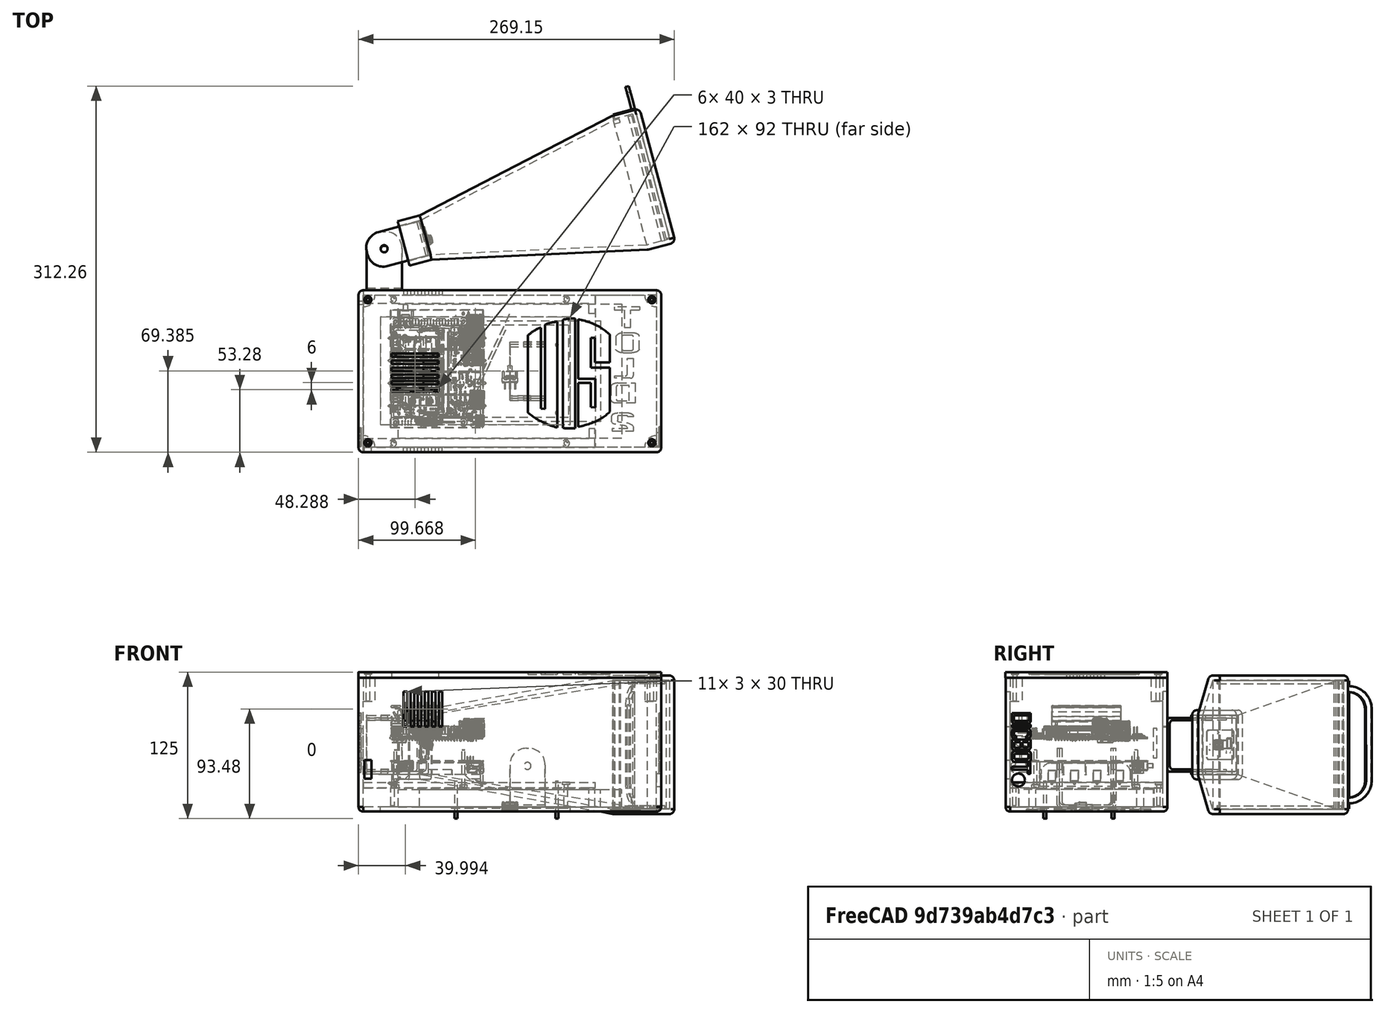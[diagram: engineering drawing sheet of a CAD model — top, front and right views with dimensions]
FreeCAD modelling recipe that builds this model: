
FCSTD DOCUMENT  (FreeCAD 0.20R)
Label: SUENCAPSULADO
License: All rights reserved
LicenseURL: http://en.wikipedia.org/wiki/All_rights_reserved
objects: Sketcher::SketchObject×38, PartDesign::Pocket×16, PartDesign::Pad×15, PartDesign::Body×9, Part::Feature×9, App::Part×6, PartDesign::Fillet×6, PartDesign::Hole×5, PartDesign::Thickness×2, Part::Compound×2, PartDesign::Plane×2
note: 148 computed .brp shape members not serialized (recipe doc carries the construction recipe); baked Part::Feature solids carry a one-line shape summary decoded from their .brp

FEATURE [Sketcher::SketchObject] Sketch
  FullyConstrained = true
  MapMode = 5
  Support = -> [XY_Plane001]
  sketch-geometry (4):
    g0: LineSegment StartX=-125 StartY=65 StartZ=0 EndX=125 EndY=65 EndZ=0
    g1: LineSegment StartX=125 StartY=65 StartZ=0 EndX=125 EndY=-65 EndZ=0
    g2: LineSegment StartX=125 StartY=-65 StartZ=0 EndX=-125 EndY=-65 EndZ=0
    g3: LineSegment StartX=-125 StartY=-65 StartZ=0 EndX=-125 EndY=65 EndZ=0
  constraints (11):
    c: Coincident(g0,g1)
    c: Coincident(g1,g2)
    c: Coincident(g2,g3)
    c: Coincident(g3,g0)
    c: Horizontal(g0)
    c: Horizontal(g2)
    c: Vertical(g1)
    c: Vertical(g3)
    c: Symmetric(g1,g0,g-1)
    c: DistanceX(g2,g2) = 250
    c: DistanceY(g1,g1) = 130
FEATURE [PartDesign::Pad] Pad
  Direction = (0,0,1)
  Length = 110
  Length2 = 10
  Profile = -> Sketch
  ReferenceAxis = -> Sketch [N_Axis]
  Type = 0
FEATURE [Sketcher::SketchObject] Sketch001
  FullyConstrained = true
  MapMode = 5
  Support = -> [XY_Plane003]
  sketch-geometry (8):
    g0: LineSegment StartX=-95.25 StartY=57.3 StartZ=0 EndX=95.25 EndY=57.3 EndZ=0
    g1: LineSegment StartX=95.25 StartY=57.3 StartZ=0 EndX=95.25 EndY=-57.3 EndZ=0
    g2: LineSegment StartX=95.25 StartY=-57.3 StartZ=0 EndX=-95.25 EndY=-57.3 EndZ=0
    g3: LineSegment StartX=-95.25 StartY=-57.3 StartZ=0 EndX=-95.25 EndY=57.3 EndZ=0
    g4: LineSegment StartX=-77.14 StartY=43.06 StartZ=0 EndX=77.14 EndY=43.06 EndZ=0
    g5: LineSegment StartX=77.14 StartY=43.06 StartZ=0 EndX=77.14 EndY=-43.06 EndZ=0
    g6: LineSegment StartX=77.14 StartY=-43.06 StartZ=0 EndX=-77.14 EndY=-43.06 EndZ=0
    g7: LineSegment StartX=-77.14 StartY=-43.06 StartZ=0 EndX=-77.14 EndY=43.06 EndZ=0
  constraints (22):
    c: Coincident(g0,g1)
    c: Coincident(g1,g2)
    c: Coincident(g2,g3)
    c: Coincident(g3,g0)
    c: Horizontal(g0)
    c: Horizontal(g2)
    c: Vertical(g1)
    c: Vertical(g3)
    c: Symmetric(g1,g0,g-1)
    c: DistanceY(g1,g1) = 114.6
    c: DistanceX(g2,g2) = 190.5
    c: Coincident(g4,g5)
    c: Coincident(g5,g6)
    c: Coincident(g6,g7)
    c: Coincident(g7,g4)
    c: Horizontal(g4)
    c: Horizontal(g6)
    c: Vertical(g5)
    c: Vertical(g7)
    c: Symmetric(g5,g4,g-1)
    c: DistanceX(g6,g6) = 154.28
    c: DistanceY(g5,g5) = 86.12
FEATURE [PartDesign::Pad] Pad001
  Direction = (0,0,1)
  Length = 15
  Length2 = 10
  Profile = -> Sketch001
  ReferenceAxis = -> Sketch001 [N_Axis]
  Type = 0
FEATURE [PartDesign::Body] Body001
  Group = -> [Sketch001,Pad001]
  Origin = -> Origin003
  Tip = -> Pad001
FEATURE [App::Part] Part001  label=""PANTALLA""
  Group = -> [Body001]
  Origin = -> Origin002
  Placement = pos=(-29,0,1) rot=(0,0,1;0rad)
FEATURE [PartDesign::Thickness] Thickness
  Base = -> Pad [Face6]
  BaseFeature = -> Pad
  Intersection = false
  Join = 0
  Mode = 0
  SupportTransform = false
  Value = 4
FEATURE [Part::Feature] Feature  label="JETSON NANO"
  Placement = pos=(-40,-44,58) rot=(0,0,1;1.5708rad)
  shape: large baked B-rep (30 MB .brp); summary skipped
FEATURE [Part::Feature] Part__Feature001  label="8SS-Dial (1)"
  shape: bbox 3.7 x 5.35 x 3.6 mm, 23 faces (baked)
FEATURE [Part::Feature] Part__Feature002  label="8SS-Terminal-PCB (Silver)"
  Placement = pos=(4.4,-9.55,0) rot=(0,1,0;1.5708rad)
  shape: bbox 0.8 x 6 x 2.8 mm, 14 faces (baked)
FEATURE [Part::Feature] Part__Feature003  label="8SS-Terminal-PCB (Silver)001"
  Placement = pos=(0,-9.55,0) rot=(0,1,0;1.5708rad)
  shape: bbox 0.8 x 6 x 2.8 mm, 14 faces (baked)
FEATURE [Part::Feature] Part__Feature004  label="8SS-Terminal-PCB (Silver)002"
  Placement = pos=(-4.4,-9.55,0) rot=(0,1,0;1.5708rad)
  shape: bbox 0.8 x 6 x 2.8 mm, 14 faces (baked)
FEATURE [Part::Feature] Part__Feature005  label="8SS-Body-3"
  shape: bbox 13 x 9.85 x 7.9 mm, 176 faces (baked)
FEATURE [App::Part] _SS1022_Z  label="8SS1022-Z"
  Group = -> [Part__Feature001,Part__Feature002,Part__Feature003,Part__Feature004,Part__Feature005]
  Origin = -> Origin004
  Placement = pos=(-32,35,-9) rot=(0,0,1;0rad)
FEATURE [Part::Feature] Part__Feature006  label="DC Power Jack 5.5mm x 2.1mm"
  Placement = pos=(-95,27,-7) rot=(-0.57735,0.57735,0.57735;4.18879rad)
  shape: bbox 14.62 x 9.77 x 14.38 mm, 201 faces, 6 solids (baked)
FEATURE [Sketcher::SketchObject] Sketch006
  FullyConstrained = true
  MapMode = 5
  Support = -> [XY_Plane006]
  sketch-geometry (4):
    g0: LineSegment StartX=-50 StartY=39.5 StartZ=0 EndX=50 EndY=39.5 EndZ=0
    g1: LineSegment StartX=50 StartY=39.5 StartZ=0 EndX=50 EndY=-39.5 EndZ=0
    g2: LineSegment StartX=50 StartY=-39.5 StartZ=0 EndX=-50 EndY=-39.5 EndZ=0
    g3: LineSegment StartX=-50 StartY=-39.5 StartZ=0 EndX=-50 EndY=39.5 EndZ=0
  constraints (11):
    c: Coincident(g0,g1)
    c: Coincident(g1,g2)
    c: Coincident(g2,g3)
    c: Coincident(g3,g0)
    c: Horizontal(g0)
    c: Horizontal(g2)
    c: Vertical(g1)
    c: Vertical(g3)
    c: Symmetric(g0,g1,g-1)
    c: DistanceX(g2,g2) = 100
    c: DistanceY(g1,g1) = 79
FEATURE [PartDesign::Pad] Pad004
  Direction = (0,0,1)
  Length = 1
  Length2 = 100
  Offset = 2
  Profile = -> Sketch006
  Refine = true
  Reversed = true
  Type = 0
FEATURE [Sketcher::SketchObject] Sketch007
  ExternalGeometry = -> [Pad004]
  FullyConstrained = true
  MapMode = 5
  Support = -> [Pad004]
  sketch-geometry (12):
    g0: Circle CenterX=-46 CenterY=22.5 CenterZ=0 NormalX=0 NormalY=0 NormalZ=1 AngleXU=0 Radius=1.25
    g1: LineSegment StartX=-46 StartY=22.5 StartZ=0 EndX=-46 EndY=39.5 EndZ=0
    g2: LineSegment StartX=-46 StartY=22.5 StartZ=0 EndX=-50 EndY=22.5 EndZ=0
    g3: Circle CenterX=40 CenterY=22.5 CenterZ=0 NormalX=0 NormalY=0 NormalZ=1 AngleXU=0 Radius=1.25
    g4: LineSegment StartX=40 StartY=22.5 StartZ=0 EndX=40 EndY=39.5 EndZ=0
    g5: LineSegment StartX=40 StartY=22.5 StartZ=0 EndX=50 EndY=22.5 EndZ=0
    g6: Circle CenterX=-46 CenterY=-35.5 CenterZ=0 NormalX=0 NormalY=0 NormalZ=1 AngleXU=0 Radius=1.25
    g7: LineSegment StartX=-46 StartY=-35.5 StartZ=0 EndX=-46 EndY=-39.5 EndZ=0
    g8: LineSegment StartX=-46 StartY=-35.5 StartZ=0 EndX=-50 EndY=-35.5 EndZ=0
    g9: Circle CenterX=40 CenterY=-35.5 CenterZ=0 NormalX=0 NormalY=0 NormalZ=1 AngleXU=0 Radius=1.25
    g10: LineSegment StartX=40 StartY=-35.5 StartZ=0 EndX=40 EndY=-39.5 EndZ=0
    g11: LineSegment StartX=40 StartY=-35.5 StartZ=0 EndX=50 EndY=-35.5 EndZ=0
  constraints (36):
    c: Coincident(g1,g0)
    c: PointOnObject(g1,g-3)
    c: Vertical(g1)
    c: DistanceY(g1,g1) = 17
    c: Radius(g0) = 1.25
    c: Coincident(g2,g0)
    c: PointOnObject(g2,g-4)
    c: Horizontal(g2)
    c: DistanceX(g2,g2) = 4
    c: Radius(g3) = 1.25
    c: Coincident(g4,g3)
    c: PointOnObject(g4,g-3)
    c: Vertical(g4)
    c: DistanceY(g4,g4) = 17
    c: Coincident(g5,g3)
    c: PointOnObject(g5,g-5)
    c: Horizontal(g5)
    c: DistanceX(g5,g5) = 10
    c: Radius(g6) = 1.25
    c: Coincident(g7,g6)
    c: PointOnObject(g7,g-6)
    c: Vertical(g7)
    c: DistanceY(g7,g7) = 4
    c: Coincident(g8,g6)
    c: PointOnObject(g8,g-4)
    c: Horizontal(g8)
    c: DistanceX(g8,g8) = 4
    c: Radius(g9) = 1.25
    c: Coincident(g10,g9)
    c: PointOnObject(g10,g-6)
    c: Vertical(g10)
    c: DistanceY(g10,g10) = 4
    c: Coincident(g11,g9)
    c: PointOnObject(g11,g-5)
    c: Horizontal(g11)
    c: DistanceX(g11,g11) = 10
FEATURE [PartDesign::Pad] Pad005
  BaseFeature = -> Pad004
  Direction = (0,0,1)
  Length = 22
  Length2 = 10
  Profile = -> Sketch007
  Refine = true
  Type = 4
FEATURE [PartDesign::Body] Body002
  Group = -> [Sketch006,Pad004,Sketch007,Pad005]
  Origin = -> Origin006
  Tip = -> Pad005
FEATURE [App::Part] Part002  label="Soporte PowerBank"
  Group = -> [Body002]
  Origin = -> Origin005
  Placement = pos=(-59,-14.6438,-12.6772) rot=(0,0,1;1.5708rad)
FEATURE [Part::Feature] Part__Feature  label="Cell Holder v5"
  Placement = pos=(-59,-17.6438,-12.6772) rot=(0,0,1;1.5708rad)
  shape: bbox 83.7 x 78.6 x 21 mm, 228 faces, 9 solids (baked)
FEATURE [Sketcher::SketchObject] Sketch017
  FullyConstrained = false
  MapMode = 5
  Support = -> [XY_Plane007]
  sketch-geometry (8):
    g0: LineSegment StartX=-125.02 StartY=68.9871 StartZ=0 EndX=125.052 EndY=68.9871 EndZ=0
    g1: LineSegment StartX=129.052 StartY=64.9871 StartZ=0 EndX=129.052 EndY=-65.0468 EndZ=0
    g2: LineSegment StartX=125.052 StartY=-69.0468 StartZ=0 EndX=-125.02 EndY=-69.0468 EndZ=0
    g3: LineSegment StartX=-129.02 StartY=-65.0468 StartZ=0 EndX=-129.02 EndY=64.9871 EndZ=0
    g4: ArcOfCircle CenterX=125.052 CenterY=-65.0468 CenterZ=0 NormalX=0 NormalY=0 NormalZ=1 AngleXU=0 Radius=4 StartAngle=4.71239 EndAngle=6.28319
    g5: ArcOfCircle CenterX=125.052 CenterY=64.9871 CenterZ=0 NormalX=0 NormalY=0 NormalZ=1 AngleXU=0 Radius=4 StartAngle=0 EndAngle=1.5708
    g6: ArcOfCircle CenterX=-125.02 CenterY=64.9871 CenterZ=0 NormalX=0 NormalY=0 NormalZ=1 AngleXU=0 Radius=4 StartAngle=1.5708 EndAngle=3.14159
    g7: ArcOfCircle CenterX=-125.02 CenterY=-65.0468 CenterZ=0 NormalX=0 NormalY=0 NormalZ=1 AngleXU=0 Radius=4 StartAngle=3.14159 EndAngle=4.71239
  constraints (16):
    c: Horizontal(g0)
    c: Horizontal(g2)
    c: Vertical(g1)
    c: Vertical(g3)
    c: Tangent(g1,g4) = 1.5708
    c: Tangent(g2,g4) = 1.5708
    c: Tangent(g0,g5) = 1.5708
    c: Tangent(g1,g5) = 1.5708
    c: Tangent(g3,g6) = 1.5708
    c: Tangent(g0,g6) = 1.5708
    c: Tangent(g3,g7) = 1.5708
    c: Tangent(g2,g7) = 1.5708
    c: Radius(g7) = 4
    c: Radius(g6) = 4
    c: Radius(g5) = 4
    c: Radius(g4) = 4
FEATURE [PartDesign::Pad] Pad012
  Direction = (0,0,1)
  Length = 5
  Length2 = 10
  Profile = -> Sketch017
  ReferenceAxis = -> Sketch017 [N_Axis]
  Type = 0
FEATURE [Sketcher::SketchObject] Sketch021
  ExternalGeometry = -> [Thickness]
  FullyConstrained = true
  MapMode = 5
  Support = -> [Thickness]
  sketch-geometry (12):
    g0: LineSegment StartX=-125 StartY=-65 StartZ=0 EndX=72.5 EndY=-65 EndZ=0
    g1: LineSegment StartX=72.5 StartY=-65 StartZ=0 EndX=72.5 EndY=-49 EndZ=0
    g2: LineSegment StartX=72.5 StartY=-49 StartZ=0 EndX=67.5 EndY=-49 EndZ=0
    g3: LineSegment StartX=67.5 StartY=-49 StartZ=0 EndX=67.5 EndY=-57.7 EndZ=0
    g4: LineSegment StartX=67.5 StartY=-57.7 StartZ=0 EndX=-125 EndY=-57.7 EndZ=0
    g5: LineSegment StartX=-125 StartY=-57.7 StartZ=0 EndX=-125 EndY=-65 EndZ=0
    g6: LineSegment StartX=-125 StartY=65 StartZ=0 EndX=72.5 EndY=65 EndZ=0
    g7: LineSegment StartX=72.5 StartY=65 StartZ=0 EndX=72.5 EndY=49 EndZ=0
    g8: LineSegment StartX=72.5 StartY=49 StartZ=0 EndX=67.5 EndY=49 EndZ=0
    g9: LineSegment StartX=67.5 StartY=49 StartZ=0 EndX=67.5 EndY=57.7 EndZ=0
    g10: LineSegment StartX=67.5 StartY=57.7 StartZ=0 EndX=-125 EndY=57.7 EndZ=0
    g11: LineSegment StartX=-125 StartY=57.7 StartZ=0 EndX=-125 EndY=65 EndZ=0
  constraints (34):
    c: Coincident(g-5,g0)
    c: PointOnObject(g0,g-5)
    c: Coincident(g0,g1)
    c: Vertical(g1)
    c: Coincident(g1,g2)
    c: Horizontal(g2)
    c: Coincident(g2,g3)
    c: Vertical(g3)
    c: Coincident(g3,g4)
    c: PointOnObject(g4,g-3)
    c: Horizontal(g4)
    c: Coincident(g4,g5)
    c: Coincident(g5,g0)
    c: DistanceY(g5,g5) = 7.3
    c: DistanceY(g1,g1) = 16
    c: DistanceX(g4,g4) = 192.5
    c: Coincident(g-4,g6)
    c: PointOnObject(g6,g-4)
    c: Coincident(g6,g7)
    c: Vertical(g7)
    c: Coincident(g7,g8)
    c: Coincident(g8,g9)
    c: Vertical(g9)
    c: Coincident(g9,g10)
    c: PointOnObject(g10,g-3)
    c: Horizontal(g10)
    c: Coincident(g10,g11)
    c: Coincident(g11,g6)
    c: DistanceX(g2,g2) = 5
    c: Horizontal(g8)
    c: DistanceX(g8,g8) = 5
    c: DistanceX(g10,g10) = 192.5
    c: DistanceY(g11,g11) = 7.3
    c: DistanceY(g7,g7) = 16
FEATURE [PartDesign::Pad] Pad017
  BaseFeature = -> Thickness
  Direction = (0,0,1)
  Length = 16
  Length2 = 10
  Profile = -> Sketch021
  ReferenceAxis = -> Sketch021 [N_Axis]
  Type = 0
FEATURE [Sketcher::SketchObject] Sketch022
  FullyConstrained = false
  MapMode = 5
  Placement = pos=(0,0,-4) rot=(1,0,0;3.14159rad)
  Support = -> [Pad017]
  sketch-geometry (4):
    g0: LineSegment StartX=51.6484 StartY=-46.3352 StartZ=0 EndX=-110.352 EndY=-46.3352 EndZ=0
    g1: LineSegment StartX=-110.352 StartY=-46.3352 StartZ=0 EndX=-110.352 EndY=45.6648 EndZ=0
    g2: LineSegment StartX=-110.352 StartY=45.6648 StartZ=0 EndX=51.6484 EndY=45.6648 EndZ=0
    g3: LineSegment StartX=51.6484 StartY=45.6648 StartZ=0 EndX=51.6484 EndY=-46.3352 EndZ=0
  constraints (10):
    c: Coincident(g0,g1)
    c: Coincident(g1,g2)
    c: Coincident(g2,g3)
    c: Coincident(g3,g0)
    c: Horizontal(g0)
    c: Horizontal(g2)
    c: Vertical(g1)
    c: Vertical(g3)
    c: DistanceX(g2,g2) = 162
    c: DistanceY(g1,g1) = 92
FEATURE [PartDesign::Pocket] Pocket
  BaseFeature = -> Pad017
  Direction = (0,0,1)
  Length = 4
  Length2 = 5
  Profile = -> Sketch022
  ReferenceAxis = -> Sketch022 [N_Axis]
  Type = 0
FEATURE [Sketcher::SketchObject] Sketch023
  ExternalGeometry = -> [Pocket]
  FullyConstrained = true
  MapMode = 5
  Placement = pos=(0,0,110) rot=(0,0,1;0rad)
  Support = -> [Pocket]
  sketch-geometry (24):
    g0: LineSegment StartX=125 StartY=-65 StartZ=0 EndX=115 EndY=-65 EndZ=0
    g1: LineSegment StartX=125 StartY=-65 StartZ=0 EndX=125 EndY=-55 EndZ=0
    g2: ArcOfCircle CenterX=125 CenterY=-65 CenterZ=0 NormalX=0 NormalY=0 NormalZ=1 AngleXU=0 Radius=10 StartAngle=1.5708 EndAngle=3.14159
    g3: Circle CenterX=121 CenterY=-61 CenterZ=0 NormalX=0 NormalY=0 NormalZ=1 AngleXU=0 Radius=1.5
    g4: LineSegment StartX=121 StartY=-61 StartZ=0 EndX=125 EndY=-61 EndZ=0
    g5: LineSegment StartX=121 StartY=-61 StartZ=0 EndX=121 EndY=-65 EndZ=0
    g6: LineSegment StartX=125 StartY=65 StartZ=0 EndX=125 EndY=55 EndZ=0
    g7: LineSegment StartX=125 StartY=65 StartZ=0 EndX=115 EndY=65 EndZ=0
    g8: ArcOfCircle CenterX=125 CenterY=65 CenterZ=0 NormalX=0 NormalY=0 NormalZ=1 AngleXU=0 Radius=10 StartAngle=3.14159 EndAngle=4.71239
    g9: Circle CenterX=121 CenterY=61 CenterZ=0 NormalX=0 NormalY=0 NormalZ=1 AngleXU=0 Radius=1.5
    g10: LineSegment StartX=121 StartY=61 StartZ=0 EndX=125 EndY=61 EndZ=0
    g11: LineSegment StartX=121 StartY=61 StartZ=0 EndX=121 EndY=65 EndZ=0
    g12: LineSegment StartX=-125 StartY=65 StartZ=0 EndX=-115 EndY=65 EndZ=0
    g13: LineSegment StartX=-125 StartY=65 StartZ=0 EndX=-125 EndY=55 EndZ=0
    g14: ArcOfCircle CenterX=-125 CenterY=65 CenterZ=0 NormalX=0 NormalY=0 NormalZ=1 AngleXU=0 Radius=10 StartAngle=4.71239 EndAngle=6.28319
    g15: Circle CenterX=-121 CenterY=61 CenterZ=0 NormalX=0 NormalY=0 NormalZ=1 AngleXU=0 Radius=1.5
    g16: LineSegment StartX=-121 StartY=61 StartZ=0 EndX=-121 EndY=65 EndZ=0
    g17: LineSegment StartX=-121 StartY=61 StartZ=0 EndX=-125 EndY=61 EndZ=0
    g18: LineSegment StartX=-125 StartY=-65 StartZ=0 EndX=-115 EndY=-65 EndZ=0
    g19: LineSegment StartX=-125 StartY=-65 StartZ=0 EndX=-125 EndY=-55 EndZ=0
    g20: ArcOfCircle CenterX=-125 CenterY=-65 CenterZ=0 NormalX=0 NormalY=0 NormalZ=1 AngleXU=0 Radius=10 StartAngle=0 EndAngle=1.5708
    g21: Circle CenterX=-121 CenterY=-61 CenterZ=0 NormalX=0 NormalY=0 NormalZ=1 AngleXU=0 Radius=1.5
    g22: LineSegment StartX=-121 StartY=-61 StartZ=0 EndX=-125 EndY=-61 EndZ=0
    g23: LineSegment StartX=-121 StartY=-61 StartZ=0 EndX=-121 EndY=-65 EndZ=0
  constraints (68):
    c: Coincident(g0,g-6)
    c: PointOnObject(g0,g-5)
    c: Coincident(g1,g0)
    c: PointOnObject(g1,g-6)
    c: DistanceY(g1,g1) = 10
    c: Coincident(g2,g0)
    c: Coincident(g2,g0)
    c: Coincident(g2,g1)
    c: Radius(g3) = 1.5
    c: Coincident(g4,g3)
    c: PointOnObject(g4,g1)
    c: Horizontal(g4)
    c: Coincident(g5,g3)
    c: PointOnObject(g5,g0)
    c: Vertical(g5)
    c: DistanceX(g4,g4) = 4
    c: DistanceY(g5,g5) = 4
    c: Coincident(g6,g-6)
    c: PointOnObject(g6,g-6)
    c: Coincident(g7,g6)
    c: PointOnObject(g7,g-3)
    c: DistanceY(g6,g6) = 10
    c: Coincident(g8,g6)
    c: Coincident(g8,g6)
    c: Coincident(g8,g7)
    c: Radius(g9) = 1.5
    c: Coincident(g10,g9)
    c: PointOnObject(g10,g6)
    c: Horizontal(g10)
    c: Coincident(g11,g9)
    c: PointOnObject(g11,g7)
    c: Vertical(g11)
    c: DistanceX(g10,g10) = 4
    c: DistanceY(g11,g11) = 4
    c: Coincident(g12,g-4)
    c: PointOnObject(g12,g-3)
    c: Coincident(g13,g12)
    c: PointOnObject(g13,g-4)
    c: DistanceX(g12,g12) = 10
    c: Coincident(g14,g12)
    c: Coincident(g14,g12)
    c: Coincident(g14,g13)
    c: Radius(g15) = 1.5
    c: Coincident(g16,g15)
    c: PointOnObject(g16,g12)
    c: Vertical(g16)
    c: Coincident(g17,g15)
    c: PointOnObject(g17,g13)
    c: Horizontal(g17)
    c: DistanceY(g16,g16) = 4
    c: DistanceX(g17,g17) = 4
    c: Coincident(g18,g-5)
    c: PointOnObject(g18,g-5)
    c: Coincident(g19,g18)
    c: PointOnObject(g19,g-4)
    c: DistanceY(g19,g19) = 10
    c: Coincident(g20,g18)
    c: Coincident(g20,g18)
    c: Coincident(g20,g19)
    c: Radius(g21) = 1.5
    c: Coincident(g22,g21)
    c: PointOnObject(g22,g19)
    c: Horizontal(g22)
    c: Coincident(g23,g21)
    c: PointOnObject(g23,g18)
    c: Vertical(g23)
    c: DistanceY(g23,g23) = 4
    c: DistanceX(g22,g22) = 4
FEATURE [PartDesign::Pad] Pad018
  BaseFeature = -> Pocket
  Direction = (0,0,1)
  Length = 20
  Length2 = 10
  Profile = -> Sketch023
  ReferenceAxis = -> Sketch023 [N_Axis]
  Reversed = true
  Type = 0
FEATURE [Sketcher::SketchObject] Sketch024
  ExternalGeometry = -> [Pad018]
  FullyConstrained = true
  MapMode = 5
  Placement = pos=(0,0,16) rot=(0,0,1;0rad)
  Support = -> [Pad018]
  sketch-geometry (12):
    g0: Circle CenterX=-100 CenterY=61.5 CenterZ=0 NormalX=0 NormalY=0 NormalZ=1 AngleXU=0 Radius=1.5
    g1: LineSegment StartX=-100 StartY=61.5 StartZ=0 EndX=-100 EndY=65 EndZ=0
    g2: LineSegment StartX=-100 StartY=61.5 StartZ=0 EndX=-125 EndY=61.5 EndZ=0
    g3: Circle CenterX=47.5 CenterY=61.5 CenterZ=0 NormalX=0 NormalY=0 NormalZ=1 AngleXU=0 Radius=1.5
    g4: LineSegment StartX=47.5 StartY=61.5 StartZ=0 EndX=47.5 EndY=65 EndZ=0
    g5: LineSegment StartX=47.5 StartY=61.5 StartZ=0 EndX=72.5 EndY=61.5 EndZ=0
    g6: Circle CenterX=-100 CenterY=-61.5 CenterZ=0 NormalX=0 NormalY=0 NormalZ=1 AngleXU=0 Radius=1.5
    g7: LineSegment StartX=-100 StartY=-61.5 StartZ=0 EndX=-125 EndY=-61.5 EndZ=0
    g8: LineSegment StartX=-100 StartY=-61.5 StartZ=0 EndX=-100 EndY=-65 EndZ=0
    g9: Circle CenterX=47.5 CenterY=-61.5 CenterZ=0 NormalX=0 NormalY=0 NormalZ=1 AngleXU=0 Radius=1.5
    g10: LineSegment StartX=47.5 StartY=-61.5 StartZ=0 EndX=72.5 EndY=-61.5 EndZ=0
    g11: LineSegment StartX=47.5 StartY=-61.5 StartZ=0 EndX=47.5 EndY=-65 EndZ=0
  constraints (36):
    c: Radius(g0) = 1.5
    c: Coincident(g1,g0)
    c: PointOnObject(g1,g-3)
    c: Vertical(g1)
    c: Coincident(g2,g0)
    c: PointOnObject(g2,g-4)
    c: Horizontal(g2)
    c: DistanceY(g1,g1) = 3.5
    c: DistanceX(g2,g2) = 25
    c: Radius(g3) = 1.5
    c: Coincident(g4,g3)
    c: PointOnObject(g4,g-3)
    c: Coincident(g5,g3)
    c: PointOnObject(g5,g-5)
    c: Horizontal(g5)
    c: Vertical(g4)
    c: DistanceX(g5,g5) = 25
    c: DistanceY(g4,g4) = 3.5
    c: Radius(g6) = 1.5
    c: Coincident(g7,g6)
    c: PointOnObject(g7,g-9)
    c: Horizontal(g7)
    c: Coincident(g8,g6)
    c: PointOnObject(g8,g-8)
    c: Vertical(g8)
    c: DistanceX(g7,g7) = 25
    c: DistanceY(g8,g8) = 3.5
    c: Radius(g9) = 1.5
    c: Coincident(g10,g9)
    c: PointOnObject(g10,g-6)
    c: Horizontal(g10)
    c: DistanceX(g10,g10) = 25
    c: Coincident(g11,g9)
    c: PointOnObject(g11,g-8)
    c: Vertical(g11)
    c: DistanceY(g11,g11) = 3.5
FEATURE [PartDesign::Pocket] Pocket004
  BaseFeature = -> Pad018
  Direction = (0,0,-1)
  Length = 15
  Length2 = 5
  Profile = -> Sketch024
  ReferenceAxis = -> Sketch024 [N_Axis]
  Type = 0
FEATURE [Sketcher::SketchObject] Sketch025
  FullyConstrained = true
  MapMode = 5
  Support = -> [XY_Plane008]
  sketch-geometry (4):
    g0: LineSegment StartX=-98.75 StartY=65 StartZ=0 EndX=98.75 EndY=65 EndZ=0
    g1: LineSegment StartX=98.75 StartY=65 StartZ=0 EndX=98.75 EndY=-65 EndZ=0
    g2: LineSegment StartX=98.75 StartY=-65 StartZ=0 EndX=-98.75 EndY=-65 EndZ=0
    g3: LineSegment StartX=-98.75 StartY=-65 StartZ=0 EndX=-98.75 EndY=65 EndZ=0
  constraints (11):
    c: Coincident(g0,g1)
    c: Coincident(g1,g2)
    c: Coincident(g2,g3)
    c: Coincident(g3,g0)
    c: Horizontal(g0)
    c: Horizontal(g2)
    c: Vertical(g1)
    c: Vertical(g3)
    c: Symmetric(g1,g0,g-1)
    c: DistanceY(g1,g1) = 130
    c: DistanceX(g2,g2) = 197.5
FEATURE [PartDesign::Pad] Pad019
  Direction = (0,0,1)
  Length = 5
  Length2 = 10
  Profile = -> Sketch025
  ReferenceAxis = -> Sketch025 [N_Axis]
  Type = 0
FEATURE [Sketcher::SketchObject] Sketch026
  ExternalGeometry = -> [Pad019]
  FullyConstrained = false
  MapMode = 5
  Placement = pos=(0,0,5) rot=(0,0,1;0rad)
  Support = -> [Pad019]
  sketch-geometry (12):
    g0: Circle CenterX=73.75 CenterY=61.4595 CenterZ=0 NormalX=0 NormalY=0 NormalZ=1 AngleXU=0 Radius=1.5
    g1: LineSegment StartX=73.75 StartY=61.4595 StartZ=0 EndX=73.8536 EndY=64.9595 EndZ=0
    g2: LineSegment StartX=73.75 StartY=61.4595 StartZ=0 EndX=98.75 EndY=61.4595 EndZ=0
    g3: Circle CenterX=-73.75 CenterY=61.446 CenterZ=0 NormalX=0 NormalY=0 NormalZ=1 AngleXU=0 Radius=1.5
    g4: LineSegment StartX=-73.75 StartY=61.446 StartZ=0 EndX=-73.75 EndY=64.946 EndZ=0
    g5: LineSegment StartX=-73.75 StartY=61.446 StartZ=0 EndX=-98.75 EndY=61.446 EndZ=0
    g6: Circle CenterX=-73.75 CenterY=-61.5 CenterZ=0 NormalX=0 NormalY=0 NormalZ=1 AngleXU=0 Radius=1.5
    g7: LineSegment StartX=-73.75 StartY=-61.5 StartZ=0 EndX=-73.75 EndY=-65 EndZ=0
    g8: LineSegment StartX=-73.75 StartY=-61.5 StartZ=0 EndX=-98.75 EndY=-61.5 EndZ=0
    g9: Circle CenterX=73.75 CenterY=-61.5 CenterZ=0 NormalX=0 NormalY=0 NormalZ=1 AngleXU=0 Radius=1.5
    g10: LineSegment StartX=73.75 StartY=-61.5 StartZ=0 EndX=98.75 EndY=-61.5 EndZ=0
    g11: LineSegment StartX=73.75 StartY=-61.5 StartZ=0 EndX=73.75 EndY=-65 EndZ=0
  constraints (33):
    c: Radius(g0) = 1.5
    c: Coincident(g1,g0)
    c: Coincident(g2,g0)
    c: PointOnObject(g2,g-3)
    c: Horizontal(g2)
    c: DistanceY(g1,g1) = 3.5
    c: DistanceX(g2,g2) = 25
    c: Radius(g3) = 1.5
    c: Coincident(g4,g3)
    c: Coincident(g5,g3)
    c: PointOnObject(g5,g-5)
    c: Horizontal(g5)
    c: Vertical(g4)
    c: DistanceX(g5,g5) = 25
    c: DistanceY(g4,g4) = 3.5
    c: Radius(g6) = 1.5
    c: Coincident(g7,g6)
    c: PointOnObject(g7,g-6)
    c: Vertical(g7)
    c: Coincident(g8,g6)
    c: PointOnObject(g8,g-5)
    c: Horizontal(g8)
    c: DistanceX(g8,g8) = 25
    c: DistanceY(g7,g7) = 3.5
    c: Radius(g9) = 1.5
    c: Coincident(g10,g9)
    c: PointOnObject(g10,g-3)
    c: Horizontal(g10)
    c: Coincident(g11,g9)
    c: PointOnObject(g11,g-6)
    c: Vertical(g11)
    c: DistanceY(g11,g11) = 3.5
    c: DistanceX(g10,g10) = 25
FEATURE [PartDesign::Hole] Hole001
  BaseFeature = -> Pad019
  CustomThreadClearance = 0
  Depth = 25
  DepthType = 0
  Diameter = 3.4
  DrillForDepth = false
  DrillPoint = 1
  DrillPointAngle = 118
  HoleCutCountersinkAngle = 90
  HoleCutCustomValues = false
  HoleCutDepth = 2.1
  HoleCutDiameter = 6.1
  HoleCutType = 1
  ModelThread = false
  Profile = -> Sketch026
  Tapered = false
  TaperedAngle = 90
  ThreadClass = 0
  ThreadDepth = 25
  ThreadDepthType = 0
  ThreadDirection = 0
  ThreadFit = 0
  ThreadSize = 9
  ThreadType = 1
  Threaded = false
  UseCustomThreadClearance = false
FEATURE [Sketcher::SketchObject] Sketch027
  FullyConstrained = false
  MapMode = 5
  Placement = pos=(0,0,0) rot=(1,0,0;3.14159rad)
  Support = -> [Hole001]
  sketch-geometry (4):
    g0: Circle CenterX=-13.5023 CenterY=43.647 CenterZ=0 NormalX=0 NormalY=0 NormalZ=1 AngleXU=0 Radius=1.25
    g1: Circle CenterX=-71.5044 CenterY=43.6503 CenterZ=0 NormalX=0 NormalY=0 NormalZ=1 AngleXU=0 Radius=1.25
    g2: Circle CenterX=-13.5092 CenterY=-42.3531 CenterZ=0 NormalX=0 NormalY=0 NormalZ=1 AngleXU=0 Radius=1.25
    g3: Circle CenterX=-71.4876 CenterY=-42.3585 CenterZ=0 NormalX=0 NormalY=0 NormalZ=1 AngleXU=0 Radius=1.25
  constraints (4):
    c: Radius(g0) = 1.25
    c: Radius(g1) = 1.25
    c: Radius(g2) = 1.25
    c: Radius(g3) = 1.25
FEATURE [PartDesign::Hole] Hole002
  BaseFeature = -> Hole001
  CustomThreadClearance = 0
  Depth = 25
  DepthType = 0
  Diameter = 2.9
  DrillForDepth = false
  DrillPoint = 1
  DrillPointAngle = 118
  HoleCutCountersinkAngle = 90
  HoleCutCustomValues = false
  HoleCutDepth = 3
  HoleCutDiameter = 6.1
  HoleCutType = 1
  ModelThread = false
  Profile = -> Sketch027
  Tapered = false
  TaperedAngle = 90
  ThreadClass = 0
  ThreadDepth = 25
  ThreadDepthType = 0
  ThreadDirection = 0
  ThreadFit = 0
  ThreadSize = 8
  ThreadType = 1
  Threaded = false
  UseCustomThreadClearance = false
FEATURE [PartDesign::Body] Body004  label="TAPA SOPORTE"
  Group = -> [Sketch025,Pad019,Sketch026,Hole001,Sketch027,Hole002]
  Origin = -> Origin008
  Placement = pos=(-26,0,16) rot=(0,0,1;0rad)
  Tip = -> Hole002
FEATURE [Sketcher::SketchObject] Sketch028
  FullyConstrained = false
  MapMode = 5
  Placement = pos=(0,0,5) rot=(0,0,1;0rad)
  Support = -> [Pad012]
  sketch-geometry (29):
    g0: LineSegment StartX=-100.732 StartY=15.1152 StartZ=0 EndX=-60.732 EndY=15.1152 EndZ=0
    g1: LineSegment StartX=-60.732 StartY=15.1152 StartZ=0 EndX=-60.732 EndY=12.1152 EndZ=0
    g2: LineSegment StartX=-60.732 StartY=12.1152 StartZ=0 EndX=-100.732 EndY=12.1152 EndZ=0
    g3: LineSegment StartX=-100.732 StartY=12.1152 StartZ=0 EndX=-100.732 EndY=15.1152 EndZ=0
    g4: LineSegment StartX=-100.732 StartY=9.11523 StartZ=0 EndX=-60.732 EndY=9.11523 EndZ=0
    g5: LineSegment StartX=-60.732 StartY=9.11523 StartZ=0 EndX=-60.732 EndY=6.11523 EndZ=0
    g6: LineSegment StartX=-60.732 StartY=6.11523 StartZ=0 EndX=-100.732 EndY=6.11523 EndZ=0
    g7: LineSegment StartX=-100.732 StartY=6.11523 StartZ=0 EndX=-100.732 EndY=9.11523 EndZ=0
    g8: LineSegment StartX=-100.732 StartY=3.11523 StartZ=0 EndX=-60.732 EndY=3.11523 EndZ=0
    g9: LineSegment StartX=-60.732 StartY=3.11523 StartZ=0 EndX=-60.732 EndY=0.115229 EndZ=0
    g10: LineSegment StartX=-60.732 StartY=0.115229 StartZ=0 EndX=-100.732 EndY=0.115229 EndZ=0
    g11: LineSegment StartX=-100.732 StartY=0.115229 StartZ=0 EndX=-100.732 EndY=3.11523 EndZ=0
    g12: LineSegment StartX=-100.732 StartY=-2.88477 StartZ=0 EndX=-60.732 EndY=-2.88477 EndZ=0
    g13: LineSegment StartX=-60.732 StartY=-2.88477 StartZ=0 EndX=-60.732 EndY=-5.88477 EndZ=0
    g14: LineSegment StartX=-60.732 StartY=-5.88477 StartZ=0 EndX=-100.732 EndY=-5.88477 EndZ=0
    g15: LineSegment StartX=-100.732 StartY=-5.88477 StartZ=0 EndX=-100.732 EndY=-2.88477 EndZ=0
    g16: LineSegment StartX=-100.732 StartY=-8.26974 StartZ=0 EndX=-60.732 EndY=-8.26974 EndZ=0
    g17: LineSegment StartX=-60.732 StartY=-8.26974 StartZ=0 EndX=-60.732 EndY=-11.2697 EndZ=0
    g18: LineSegment StartX=-60.732 StartY=-11.2697 StartZ=0 EndX=-100.732 EndY=-11.2697 EndZ=0
    g19: LineSegment StartX=-100.732 StartY=-11.2697 StartZ=0 EndX=-100.732 EndY=-8.26974 EndZ=0
    g20: LineSegment StartX=-100.732 StartY=-14.2697 StartZ=0 EndX=-60.732 EndY=-14.2697 EndZ=0
    g21: LineSegment StartX=-60.732 StartY=-14.2697 StartZ=0 EndX=-60.732 EndY=-17.2697 EndZ=0
    g22: LineSegment StartX=-60.732 StartY=-17.2697 StartZ=0 EndX=-100.732 EndY=-17.2697 EndZ=0
    g23: LineSegment StartX=-100.732 StartY=-17.2697 StartZ=0 EndX=-100.732 EndY=-14.2697 EndZ=0
    g24: LineSegment StartX=-100.732 StartY=12.1152 StartZ=0 EndX=-100.732 EndY=9.11523 EndZ=0
    g25: LineSegment StartX=-100.732 StartY=6.11523 StartZ=0 EndX=-100.732 EndY=3.11523 EndZ=0
    g26: LineSegment StartX=-100.732 StartY=0.115229 StartZ=0 EndX=-100.732 EndY=-2.88477 EndZ=0
    g27: LineSegment StartX=-100.732 StartY=-5.88477 StartZ=0 EndX=-100.732 EndY=-8.26974 EndZ=0
    g28: LineSegment StartX=-100.732 StartY=-11.2697 StartZ=0 EndX=-100.732 EndY=-14.2697 EndZ=0
  constraints (79):
    c: Coincident(g0,g1)
    c: Coincident(g1,g2)
    c: Coincident(g2,g3)
    c: Coincident(g3,g0)
    c: Horizontal(g0)
    c: Horizontal(g2)
    c: Vertical(g1)
    c: Vertical(g3)
    c: Coincident(g4,g5)
    c: Coincident(g5,g6)
    c: Coincident(g6,g7)
    c: Coincident(g7,g4)
    c: Horizontal(g4)
    c: Horizontal(g6)
    c: Vertical(g5)
    c: Vertical(g7)
    c: Coincident(g8,g9)
    c: Coincident(g9,g10)
    c: Coincident(g10,g11)
    c: Coincident(g11,g8)
    c: Horizontal(g8)
    c: Horizontal(g10)
    c: Vertical(g9)
    c: Vertical(g11)
    c: Coincident(g12,g13)
    c: Coincident(g13,g14)
    c: Coincident(g14,g15)
    c: Coincident(g15,g12)
    c: Horizontal(g12)
    c: Horizontal(g14)
    c: Vertical(g13)
    c: Vertical(g15)
    c: Coincident(g16,g17)
    c: Coincident(g17,g18)
    c: Coincident(g18,g19)
    c: Coincident(g19,g16)
    c: Horizontal(g16)
    c: Horizontal(g18)
    c: Vertical(g17)
    c: Vertical(g19)
    c: Coincident(g20,g21)
    c: Coincident(g21,g22)
    c: Coincident(g22,g23)
    c: Coincident(g23,g20)
    c: Horizontal(g20)
    c: Horizontal(g22)
    c: Vertical(g21)
    c: Vertical(g23)
    c: DistanceX(g0,g0) = 40
    c: DistanceX(g4,g4) = 40
    c: DistanceX(g8,g8) = 40
    c: DistanceX(g12,g12) = 40
    c: DistanceX(g16,g16) = 40
    c: DistanceX(g20,g20) = 40
    c: Coincident(g24,g2)
    c: Coincident(g24,g4)
    c: Vertical(g24)
    c: Coincident(g25,g6)
    c: Coincident(g25,g8)
    c: Vertical(g25)
    c: Coincident(g26,g10)
    c: Coincident(g26,g12)
    c: Vertical(g26)
    c: Coincident(g27,g14)
    c: Coincident(g27,g16)
    c: Coincident(g28,g18)
    c: Coincident(g28,g20)
    c: Vertical(g28)
    c: Vertical(g27)
    c: DistanceY(g3,g3) = 3
    c: DistanceY(g24,g24) = 3
    c: DistanceY(g7,g7) = 3
    c: DistanceY(g25,g25) = 3
    c: DistanceY(g11,g11) = 3
    c: DistanceY(g26,g26) = 3
    c: DistanceY(g15,g15) = 3
    c: DistanceY(g19,g19) = 3
    c: DistanceY(g28,g28) = 3
    c: DistanceY(g23,g23) = 3
FEATURE [PartDesign::Pocket] Pocket005
  BaseFeature = -> Pad012
  Direction = (0,0,-1)
  Length = 5
  Length2 = 5
  Profile = -> Sketch028
  ReferenceAxis = -> Sketch028 [N_Axis]
  Type = 0
FEATURE [Sketcher::SketchObject] Sketch029
  FullyConstrained = false
  MapMode = 5
  Placement = pos=(0,0,-4) rot=(1,0,0;3.14159rad)
  Support = -> [Pocket004]
  sketch-geometry (136):
    g0: LineSegment StartX=110.986 StartY=-52.3711 StartZ=0 EndX=110.986 EndY=-54.9507 EndZ=0
    g1: LineSegment StartX=110.986 StartY=-54.9507 StartZ=0 EndX=89.0206 EndY=-54.9507 EndZ=0
    g2: LineSegment StartX=89.0206 StartY=-54.9507 StartZ=0 EndX=89.0206 EndY=-52.2929 EndZ=0
    g3: LineSegment StartX=89.0206 StartY=-52.2929 StartZ=0 EndX=97.5411 EndY=-52.2929 EndZ=0
    g4: LineSegment StartX=97.5411 StartY=-52.2929 StartZ=0 EndX=97.5411 EndY=-37.2844 EndZ=0
    g5: LineSegment StartX=97.5411 StartY=-37.2844 StartZ=0 EndX=103.013 EndY=-37.2844 EndZ=0
    g6: LineSegment StartX=103.013 StartY=-37.2844 StartZ=0 EndX=103.013 EndY=-52.3711 EndZ=0
    g7: LineSegment StartX=103.013 StartY=-52.3711 StartZ=0 EndX=110.986 EndY=-52.3711 EndZ=0
    g8: LineSegment StartX=104.118 StartY=-30.5505 StartZ=0 EndX=96.7981 EndY=-30.5505 EndZ=0
    g9: LineSegment StartX=95.2981 StartY=-29.0505 StartZ=0 EndX=95.2981 EndY=-19.3098 EndZ=0
    g10: LineSegment StartX=96.7981 StartY=-17.8098 StartZ=0 EndX=103.848 EndY=-17.8098 EndZ=0
    g11: LineSegment StartX=105.348 StartY=-19.3098 StartZ=0 EndX=105.348 EndY=-29.3197 EndZ=0
    g12: ArcOfCircle CenterX=96.7981 CenterY=-29.0505 CenterZ=0 NormalX=0 NormalY=0 NormalZ=1 AngleXU=0 Radius=1.5 StartAngle=3.14159 EndAngle=4.71239
    g13: ArcOfCircle CenterX=96.7981 CenterY=-19.3098 CenterZ=0 NormalX=0 NormalY=0 NormalZ=1 AngleXU=0 Radius=1.5 StartAngle=1.5708 EndAngle=3.14159
    g14: ArcOfCircle CenterX=103.848 CenterY=-19.3098 CenterZ=0 NormalX=0 NormalY=0 NormalZ=1 AngleXU=0 Radius=1.5 StartAngle=1e-16 EndAngle=1.5708
    g15: ArcOfCircle CenterX=104.118 CenterY=-29.3197 CenterZ=0 NormalX=0 NormalY=0 NormalZ=1 AngleXU=0 Radius=1.23076 StartAngle=4.71239 EndAngle=6.28319
    g16: LineSegment StartX=90.2078 StartY=-29.7136 StartZ=0 EndX=90.2078 EndY=-18.6789 EndZ=0
    g17: LineSegment StartX=96.7618 StartY=-15.6424 StartZ=0 EndX=103.914 EndY=-15.6424 EndZ=0
    g18: LineSegment StartX=110.388 StartY=-18.6753 StartZ=0 EndX=110.388 EndY=-29.7035 EndZ=0
    g19: LineSegment StartX=104.313 StartY=-32.7242 StartZ=0 EndX=96.4457 EndY=-32.7242 EndZ=0
    g20-g23: Circle x4 (B-spline internal-alignment scaffolding for g24; pole/knot coordinates omitted)
    g24: BSplineCurve PolesCount=4 KnotsCount=2 Degree=3 IsPeriodic=0
    g25: GeomPoint X=110.388 Y=-29.7035 Z=0
    g26: GeomPoint X=104.313 Y=-32.7242 Z=0
    g27-g30: Circle x4 (B-spline internal-alignment scaffolding for g31; pole/knot coordinates omitted)
    g31: BSplineCurve PolesCount=4 KnotsCount=2 Degree=3 IsPeriodic=0
    g32: GeomPoint X=96.4457 Y=-32.7242 Z=0
    g33: GeomPoint X=90.2078 Y=-29.7136 Z=0
    g34-g37: Circle x4 (B-spline internal-alignment scaffolding for g38; pole/knot coordinates omitted)
    g38: BSplineCurve PolesCount=4 KnotsCount=2 Degree=3 IsPeriodic=0
    g39: GeomPoint X=96.7618 Y=-15.6424 Z=0
    g40: GeomPoint X=90.2078 Y=-18.6789 Z=0
    g41-g44: Circle x4 (B-spline internal-alignment scaffolding for g45; pole/knot coordinates omitted)
    g45: BSplineCurve PolesCount=4 KnotsCount=2 Degree=3 IsPeriodic=0
    g46: GeomPoint X=110.388 Y=-18.6753 Z=0
    g47: GeomPoint X=103.914 Y=-15.6424 Z=0
    g48: LineSegment StartX=100.094 StartY=2.20614 StartZ=0 EndX=100.094 EndY=-10.8526 EndZ=0
    g49: LineSegment StartX=100.094 StartY=-10.8526 StartZ=0 EndX=105.196 EndY=-10.8526 EndZ=0
    g50: LineSegment StartX=105.196 StartY=-10.8526 StartZ=0 EndX=105.196 EndY=3.59963 EndZ=0
    g51: LineSegment StartX=102.82 StartY=5.97588 StartZ=0 EndX=89.1724 EndY=5.97588 EndZ=0
    g52: LineSegment StartX=89.1724 StartY=5.97588 StartZ=0 EndX=89.1724 EndY=4.00333 EndZ=0
    g53: LineSegment StartX=89.1724 StartY=4.00333 StartZ=0 EndX=98.2966 EndY=4.00333 EndZ=0
    g54: ArcOfCircle CenterX=102.82 CenterY=3.59963 CenterZ=0 NormalX=0 NormalY=0 NormalZ=1 AngleXU=0 Radius=2.37625 StartAngle=0 EndAngle=1.5708
    g55: ArcOfCircle CenterX=98.2966 CenterY=2.20614 CenterZ=0 NormalX=0 NormalY=0 NormalZ=1 AngleXU=0 Radius=1.79718 StartAngle=0 EndAngle=1.5708
    g56: LineSegment StartX=91.8795 StartY=10.0455 StartZ=0 EndX=106.797 EndY=10.0455 EndZ=0
    g57: LineSegment StartX=106.797 StartY=10.0455 StartZ=0 EndX=106.797 EndY=27.1487 EndZ=0
    g58: LineSegment StartX=106.797 StartY=27.1487 StartZ=0 EndX=89.9249 EndY=27.1487 EndZ=0
    g59: LineSegment StartX=86.1157 StartY=13.137 StartZ=0 EndX=86.1157 EndY=24.7171 EndZ=0
    g60-g63: Circle x4 (B-spline internal-alignment scaffolding for g64; pole/knot coordinates omitted)
    g64: BSplineCurve PolesCount=4 KnotsCount=2 Degree=3 IsPeriodic=0
    g65: GeomPoint X=91.8795 Y=10.0455 Z=0
    g66: GeomPoint X=86.1157 Y=13.137 Z=0
    g67-g70: Circle x4 (B-spline internal-alignment scaffolding for g71; pole/knot coordinates omitted)
    g71: BSplineCurve PolesCount=4 KnotsCount=2 Degree=3 IsPeriodic=0
    g72: GeomPoint X=89.9249 Y=27.1487 Z=0
    g73: GeomPoint X=86.1157 Y=24.7171 Z=0
    g74: LineSegment StartX=101.686 StartY=12.0747 StartZ=0 EndX=92.2402 EndY=12.0747 EndZ=0
    g75: LineSegment StartX=90.7402 StartY=13.5747 StartZ=0 EndX=90.7402 EndY=23.7644 EndZ=0
    g76: LineSegment StartX=92.2402 StartY=25.2644 StartZ=0 EndX=101.686 EndY=25.2644 EndZ=0
    g77: LineSegment StartX=101.686 StartY=25.2644 StartZ=0 EndX=101.686 EndY=12.0747 EndZ=0
    g78: ArcOfCircle CenterX=92.2402 CenterY=13.5747 CenterZ=0 NormalX=0 NormalY=0 NormalZ=1 AngleXU=0 Radius=1.5 StartAngle=3.14159 EndAngle=4.71239
    g79: ArcOfCircle CenterX=92.2402 CenterY=23.7644 CenterZ=0 NormalX=0 NormalY=0 NormalZ=1 AngleXU=0 Radius=1.5 StartAngle=1.5708 EndAngle=3.14159
    g80: LineSegment StartX=105.602 StartY=38.7279 StartZ=0 EndX=100.525 EndY=38.7279 EndZ=0
    g81: LineSegment StartX=99.237 StartY=37.8542 StartZ=0 EndX=92.871 EndY=37.8542 EndZ=0
    g82: LineSegment StartX=100.638 StartY=35.747 StartZ=0 EndX=92.0327 EndY=35.747 EndZ=0
    g83: LineSegment StartX=91.8168 StartY=39.0069 StartZ=0 EndX=91.8168 EndY=41.9573 EndZ=0
    g84: LineSegment StartX=100.462 StartY=48.8833 StartZ=0 EndX=87.1153 EndY=48.8833 EndZ=0
    g85: LineSegment StartX=87.1153 StartY=48.8833 StartZ=0 EndX=87.1153 EndY=51.061 EndZ=0
    g86: LineSegment StartX=86.5606 StartY=38.4803 StartZ=0 EndX=86.5606 EndY=42.551 EndZ=0
    g87: LineSegment StartX=87.1153 StartY=51.061 StartZ=0 EndX=105.637 EndY=51.061 EndZ=0
    g88-g91: Circle x4 (B-spline internal-alignment scaffolding for g92; pole/knot coordinates omitted)
    g92: BSplineCurve PolesCount=4 KnotsCount=2 Degree=3 IsPeriodic=0
    g93: GeomPoint X=105.602 Y=38.7279 Z=0
    g94: GeomPoint X=100.638 Y=35.747 Z=0
    g95-g98: Circle x4 (B-spline internal-alignment scaffolding for g99; pole/knot coordinates omitted)
    g99: BSplineCurve PolesCount=4 KnotsCount=2 Degree=3 IsPeriodic=0
    g100: GeomPoint X=100.525 Y=38.7279 Z=0
    g101: GeomPoint X=99.237 Y=37.8542 Z=0
    g102: Circle CenterX=92.871 CenterY=37.8542 CenterZ=0 NormalX=0 NormalY=0 NormalZ=1 AngleXU=0 Radius=1
    g103: Circle CenterX=91.848 CenterY=38.002 CenterZ=0 NormalX=0 NormalY=0 NormalZ=1 AngleXU=0 Radius=1
    g104: Circle CenterX=91.8168 CenterY=39.0069 CenterZ=0 NormalX=0 NormalY=0 NormalZ=1 AngleXU=0 Radius=1
    g105: BSplineCurve PolesCount=3 KnotsCount=2 Degree=2 IsPeriodic=0
    g106: GeomPoint X=92.871 Y=37.8542 Z=0
    g107: GeomPoint X=91.8168 Y=39.0069 Z=0
    g108-g111: Circle x4 (B-spline internal-alignment scaffolding for g112; pole/knot coordinates omitted)
    g112: BSplineCurve PolesCount=4 KnotsCount=2 Degree=3 IsPeriodic=0
    g113: GeomPoint X=92.0327 Y=35.747 Z=0
    g114: GeomPoint X=86.5606 Y=38.4803 Z=0
    g115-g119: Circle x5 (B-spline internal-alignment scaffolding for g120; pole/knot coordinates omitted)
    g120: BSplineCurve PolesCount=5 KnotsCount=3 Degree=3 IsPeriodic=0
    g121: GeomPoint X=105.637 Y=47.7343 Z=0
    g122: GeomPoint X=98.4747 Y=43.9488 Z=0
    g123: GeomPoint X=91.8168 Y=41.9573 Z=0
    g124-g129: Circle x6 (B-spline internal-alignment scaffolding for g130; pole/knot coordinates omitted)
    g130: BSplineCurve PolesCount=6 KnotsCount=4 Degree=3 IsPeriodic=0
    g131-g134: GeomPoint x4 (B-spline internal-alignment scaffolding for g130; pole/knot coordinates omitted)
    g135: LineSegment StartX=105.637 StartY=51.061 StartZ=0 EndX=105.637 EndY=47.7343 EndZ=0
  constraints (183):
    c: Vertical(g0)
    c: Coincident(g0,g1)
    c: Horizontal(g1)
    c: Coincident(g1,g2)
    c: Vertical(g2)
    c: Coincident(g2,g3)
    c: Horizontal(g3)
    c: Coincident(g3,g4)
    c: Vertical(g4)
    c: Coincident(g4,g5)
    c: Horizontal(g5)
    c: Coincident(g5,g6)
    c: Vertical(g6)
    c: Coincident(g6,g7)
    c: Coincident(g7,g0)
    c: Horizontal(g7)
    c: Horizontal(g8)
    c: Horizontal(g10)
    c: Vertical(g9)
    c: Vertical(g11)
    c: Tangent(g8,g12) = 1.5708
    c: Tangent(g9,g12) = 1.5708
    c: Tangent(g10,g13) = 1.5708
    c: Tangent(g9,g13) = 1.5708
    c: Tangent(g11,g14) = 1.5708
    c: Tangent(g10,g14) = 1.5708
    c: Tangent(g11,g15) = 1.5708
    c: Tangent(g8,g15) = 1.5708
    c: Equal(g12,g13)
    c: Equal(g13,g14)
    c: Vertical(g16)
    c: Horizontal(g17)
    c: Vertical(g18)
    c: Horizontal(g19)
    c: Weight(g20) = 1
    c: Coincident(g24,g18)
    c: Equal(g20,g21)
    c: Equal(g20,g22)
    c: Equal(g20,g23)
    c: Coincident(g24,g19)
    c: InternalAlignment(g20-g23 -> g24) x4
    c: InternalAlignment(g25,g24)
    c: InternalAlignment(g26,g24)
    c: Weight(g27) = 1
    c: Coincident(g31,g19)
    c: Equal(g27,g28)
    c: Equal(g27,g29)
    c: Equal(g27,g30)
    c: Coincident(g31,g16)
    c: InternalAlignment(g27-g30 -> g31) x4
    c: InternalAlignment(g32,g31)
    c: InternalAlignment(g33,g31)
    c: Weight(g34) = 1
    c: Coincident(g38,g17)
    c: Equal(g34,g35)
    c: Equal(g34,g36)
    c: Equal(g34,g37)
    c: Coincident(g38,g16)
    c: InternalAlignment(g34-g37 -> g38) x4
    c: InternalAlignment(g39,g38)
    c: InternalAlignment(g40,g38)
    c: Weight(g41) = 1
    c: Coincident(g45,g18)
    c: Equal(g41,g42)
    c: Equal(g41,g43)
    c: Equal(g41,g44)
    c: Coincident(g45,g17)
    c: InternalAlignment(g41-g44 -> g45) x4
    c: InternalAlignment(g46,g45)
    c: InternalAlignment(g47,g45)
    c: Vertical(g48)
    c: Coincident(g48,g49)
    c: Horizontal(g49)
    c: Coincident(g49,g50)
    c: Horizontal(g51)
    c: Coincident(g51,g52)
    c: Coincident(g52,g53)
    c: Vertical(g50)
    c: Horizontal(g53)
    c: Vertical(g52)
    c: Tangent(g50,g54) = -1.5708
    c: Tangent(g51,g54) = -1.5708
    c: Tangent(g48,g55) = 1.5708
    c: Tangent(g53,g55) = 1.5708
    c: Horizontal(g56)
    c: Coincident(g56,g57)
    c: Vertical(g57)
    c: Coincident(g57,g58)
    c: Horizontal(g58)
    c: Vertical(g59)
    c: Weight(g60) = 1
    c: Coincident(g64,g56)
    c: Equal(g60,g61)
    c: Equal(g60,g62)
    c: Equal(g60,g63)
    c: Coincident(g64,g59)
    c: InternalAlignment(g60-g63 -> g64) x4
    c: InternalAlignment(g65,g64)
    c: InternalAlignment(g66,g64)
    c: Weight(g67) = 1
    c: Coincident(g71,g58)
    c: Equal(g67,g68)
    c: Equal(g67,g69)
    c: Equal(g67,g70)
    c: Coincident(g71,g59)
    c: InternalAlignment(g67-g70 -> g71) x4
    c: InternalAlignment(g72,g71)
    c: InternalAlignment(g73,g71)
    c: Coincident(g76,g77)
    c: Coincident(g77,g74)
    c: Horizontal(g74)
    c: Horizontal(g76)
    c: Vertical(g75)
    c: Vertical(g77)
    c: Tangent(g74,g78) = 1.5708
    c: Tangent(g75,g78) = 1.5708
    c: Tangent(g76,g79) = 1.5708
    c: Tangent(g75,g79) = 1.5708
    c: Radius(g78) = 1.5
    c: Radius(g79) = 1.5
    c: Horizontal(g80)
    c: Horizontal(g81)
    c: Horizontal(g82)
    c: Horizontal(g84)
    c: Coincident(g85,g84)
    c: Vertical(g86)
    c: Vertical(g83)
    c: Vertical(g85)
    c: Coincident(g87,g85)
    c: Horizontal(g87)
    c: Weight(g88) = 1
    c: Coincident(g92,g80)
    c: Equal(g88,g89)
    c: Equal(g88,g90)
    c: Equal(g88,g91)
    c: Coincident(g92,g82)
    c: InternalAlignment(g88-g91 -> g92) x4
    c: InternalAlignment(g93,g92)
    c: InternalAlignment(g94,g92)
    c: Weight(g95) = 1
    c: Coincident(g99,g80)
    c: Equal(g95,g96)
    c: Equal(g95,g97)
    c: Equal(g95,g98)
    c: Coincident(g99,g81)
    c: InternalAlignment(g95-g98 -> g99) x4
    c: InternalAlignment(g100,g99)
    c: InternalAlignment(g101,g99)
    c: Weight(g102) = 1
    c: Coincident(g105,g81)
    c: Equal(g102,g103)
    c: Equal(g102,g104)
    c: Coincident(g105,g83)
    c: InternalAlignment(g102,g105)
    c: InternalAlignment(g103,g105)
    c: InternalAlignment(g104,g105)
    c: InternalAlignment(g106,g105)
    c: InternalAlignment(g107,g105)
    c: Weight(g108) = 1
    c: Coincident(g112,g82)
    c: Equal(g108,g109)
    c: Equal(g108,g110)
    c: Equal(g108,g111)
    c: Coincident(g112,g86)
    c: InternalAlignment(g108-g111 -> g112) x4
    c: InternalAlignment(g113,g112)
    c: InternalAlignment(g114,g112)
    c: Weight(g115) = 1
    c: Equal(g115, g116-g119) x4
    c: Coincident(g120,g83)
    c: InternalAlignment(g115-g119 -> g120) x5
    c: InternalAlignment(g121,g120)
    c: InternalAlignment(g122,g120)
    c: InternalAlignment(g123,g120)
    c: Weight(g124) = 1
    c: Coincident(g130,g84)
    c: Equal(g124, g125-g129) x5
    c: Coincident(g130,g86)
    c: InternalAlignment(g124-g129 -> g130) x6
    c: InternalAlignment(g131-g134 -> g130) x4
    c: Coincident(g135,g87)
    c: Coincident(g135,g120)
    c: Vertical(g135)
FEATURE [PartDesign::Pocket] Pocket006
  BaseFeature = -> Pocket004
  Direction = (0,0,1)
  Length = 2
  Length2 = 5
  Profile = -> Sketch029
  ReferenceAxis = -> Sketch029 [N_Axis]
  Type = 0
FEATURE [Sketcher::SketchObject] Sketch030
  FullyConstrained = false
  MapMode = 5
  Placement = pos=(0,0,5) rot=(0,0,1;0rad)
  Support = -> [Pocket005]
  sketch-geometry (64):
    g0: LineSegment StartX=26.3615 StartY=37.1956 StartZ=0 EndX=26.3615 EndY=-31.8592 EndZ=0
    g1: LineSegment StartX=26.3615 StartY=-31.8592 StartZ=0 EndX=29.97 EndY=-32.1873 EndZ=0
    g2: LineSegment StartX=29.97 StartY=-32.1873 StartZ=0 EndX=29.97 EndY=39.656 EndZ=0
    g3: LineSegment StartX=40.3036 StartY=42.1163 StartZ=0 EndX=40.3036 EndY=-48.0978 EndZ=0
    g4: LineSegment StartX=15.3717 StartY=30.4705 StartZ=0 EndX=15.3717 EndY=-35.3038 EndZ=0
    g5: LineSegment StartX=45.3002 StartY=44.0847 StartZ=0 EndX=45.3002 EndY=-48.3978 EndZ=0
    g6: LineSegment StartX=55.7798 StartY=44.7948 StartZ=0 EndX=55.7798 EndY=-48.5358 EndZ=0
    g7: Circle CenterX=15.3717 CenterY=30.4705 CenterZ=0 NormalX=0 NormalY=0 NormalZ=1 AngleXU=0 Radius=1
    g8: Circle CenterX=20.3043 CenterY=35.1328 CenterZ=0 NormalX=0 NormalY=0 NormalZ=1 AngleXU=0 Radius=1
    g9: Circle CenterX=26.3615 CenterY=37.1956 CenterZ=0 NormalX=0 NormalY=0 NormalZ=1 AngleXU=0 Radius=1
    g10: BSplineCurve PolesCount=3 KnotsCount=2 Degree=2 IsPeriodic=0
    g11: GeomPoint X=15.3717 Y=30.4705 Z=0
    g12: GeomPoint X=26.3615 Y=37.1956 Z=0
    g13: Circle CenterX=29.97 CenterY=39.656 CenterZ=0 NormalX=0 NormalY=0 NormalZ=1 AngleXU=0 Radius=1
    g14: Circle CenterX=35.0446 CenterY=41.9133 CenterZ=0 NormalX=0 NormalY=0 NormalZ=1 AngleXU=0 Radius=1
    g15: Circle CenterX=40.3036 CenterY=42.1163 CenterZ=0 NormalX=0 NormalY=0 NormalZ=1 AngleXU=0 Radius=1
    g16: BSplineCurve PolesCount=3 KnotsCount=2 Degree=2 IsPeriodic=0
    g17: GeomPoint X=29.97 Y=39.656 Z=0
    g18: GeomPoint X=40.3036 Y=42.1163 Z=0
    g19: Circle CenterX=45.3002 CenterY=44.0847 CenterZ=0 NormalX=0 NormalY=0 NormalZ=1 AngleXU=0 Radius=1
    g20: Circle CenterX=51.3415 CenterY=45.0886 CenterZ=0 NormalX=0 NormalY=0 NormalZ=1 AngleXU=0 Radius=1
    g21: Circle CenterX=55.7798 CenterY=44.7948 CenterZ=0 NormalX=0 NormalY=0 NormalZ=1 AngleXU=0 Radius=1
    g22: BSplineCurve PolesCount=3 KnotsCount=2 Degree=2 IsPeriodic=0
    g23: GeomPoint X=45.3002 Y=44.0847 Z=0
    g24: GeomPoint X=55.7798 Y=44.7948 Z=0
    g25: Circle CenterX=15.3717 CenterY=-35.3038 CenterZ=0 NormalX=0 NormalY=0 NormalZ=1 AngleXU=0 Radius=1
    g26: Circle CenterX=24.4025 CenterY=-43.2598 CenterZ=0 NormalX=0 NormalY=0 NormalZ=1 AngleXU=0 Radius=1
    g27: Circle CenterX=40.3036 CenterY=-48.0978 CenterZ=0 NormalX=0 NormalY=0 NormalZ=1 AngleXU=0 Radius=1
    g28: BSplineCurve PolesCount=3 KnotsCount=2 Degree=2 IsPeriodic=0
    g29: GeomPoint X=15.3717 Y=-35.3038 Z=0
    g30: GeomPoint X=40.3036 Y=-48.0978 Z=0
    g31: Circle CenterX=45.3002 CenterY=-48.3978 CenterZ=0 NormalX=0 NormalY=0 NormalZ=1 AngleXU=0 Radius=1
    g32: Circle CenterX=50.4876 CenterY=-49.1388 CenterZ=0 NormalX=0 NormalY=0 NormalZ=1 AngleXU=0 Radius=1
    g33: Circle CenterX=55.7798 CenterY=-48.5358 CenterZ=0 NormalX=0 NormalY=0 NormalZ=1 AngleXU=0 Radius=1
    g34: BSplineCurve PolesCount=3 KnotsCount=2 Degree=2 IsPeriodic=0
    g35: GeomPoint X=45.3002 Y=-48.3978 Z=0
    g36: GeomPoint X=55.7798 Y=-48.5358 Z=0
    g37: LineSegment StartX=58.0863 StartY=44.3344 StartZ=0 EndX=58.0863 EndY=-6.56948 EndZ=0
    g38: LineSegment StartX=58.0863 StartY=-6.56948 StartZ=0 EndX=72.8302 EndY=-6.56948 EndZ=0
    g39: LineSegment StartX=72.8302 StartY=-6.56948 StartZ=0 EndX=72.8302 EndY=-30.8628 EndZ=0
    g40: LineSegment StartX=72.8302 StartY=-30.8628 StartZ=0 EndX=69.0746 EndY=-30.7154 EndZ=0
    g41: LineSegment StartX=69.0746 StartY=-30.7154 StartZ=0 EndX=69.0746 EndY=-10.0834 EndZ=0
    g42: LineSegment StartX=69.0746 StartY=-10.0834 StartZ=0 EndX=58.1125 EndY=-10.0834 EndZ=0
    g43: LineSegment StartX=58.1125 StartY=-10.0834 StartZ=0 EndX=58.1125 EndY=-47.3498 EndZ=0
    g44: LineSegment StartX=85.2152 StartY=-34.4005 StartZ=0 EndX=85.2152 EndY=3.08587 EndZ=0
    g45: LineSegment StartX=85.2152 StartY=3.08587 StartZ=0 EndX=68.9374 EndY=3.08587 EndZ=0
    g46: LineSegment StartX=68.9374 StartY=3.08587 StartZ=0 EndX=68.9374 EndY=28.5349 EndZ=0
    g47: LineSegment StartX=68.9374 StartY=28.5349 StartZ=0 EndX=69.0126 EndY=28.5349 EndZ=0
    g48: LineSegment StartX=69.0126 StartY=28.5349 StartZ=0 EndX=72.5502 EndY=28.5349 EndZ=0
    g49: LineSegment StartX=72.5502 StartY=28.5349 StartZ=0 EndX=72.5502 EndY=7.45628 EndZ=0
    g50: LineSegment StartX=72.5502 StartY=7.45628 StartZ=0 EndX=85.1532 EndY=7.45628 EndZ=0
    g51: LineSegment StartX=85.1532 StartY=7.45628 StartZ=0 EndX=85.1532 EndY=31.1882 EndZ=0
    g52: Circle CenterX=58.0863 CenterY=44.3344 CenterZ=0 NormalX=0 NormalY=0 NormalZ=1 AngleXU=0 Radius=1
    g53: Circle CenterX=75.3142 CenterY=40.9823 CenterZ=0 NormalX=0 NormalY=0 NormalZ=1 AngleXU=0 Radius=1
    g54: Circle CenterX=85.1532 CenterY=31.1882 CenterZ=0 NormalX=0 NormalY=0 NormalZ=1 AngleXU=0 Radius=1
    g55: BSplineCurve PolesCount=3 KnotsCount=2 Degree=2 IsPeriodic=0
    g56: GeomPoint X=58.0863 Y=44.3344 Z=0
    g57: GeomPoint X=85.1532 Y=31.1882 Z=0
    g58: Circle CenterX=58.1125 CenterY=-47.3498 CenterZ=0 NormalX=0 NormalY=0 NormalZ=1 AngleXU=0 Radius=1
    g59: Circle CenterX=76.5881 CenterY=-43.7493 CenterZ=0 NormalX=0 NormalY=0 NormalZ=1 AngleXU=0 Radius=1
    g60: Circle CenterX=85.2152 CenterY=-34.4005 CenterZ=0 NormalX=0 NormalY=0 NormalZ=1 AngleXU=0 Radius=1
    g61: BSplineCurve PolesCount=3 KnotsCount=2 Degree=2 IsPeriodic=0
    g62: GeomPoint X=58.1125 Y=-47.3498 Z=0
    g63: GeomPoint X=85.2152 Y=-34.4005 Z=0
  constraints (105):
    c: Vertical(g0)
    c: Coincident(g0,g1)
    c: Coincident(g1,g2)
    c: Vertical(g2)
    c: Vertical(g3)
    c: Vertical(g4)
    c: Vertical(g5)
    c: Vertical(g6)
    c: Weight(g7) = 1
    c: Coincident(g10,g4)
    c: Equal(g7,g8)
    c: Equal(g7,g9)
    c: Coincident(g10,g0)
    c: InternalAlignment(g7,g10)
    c: InternalAlignment(g8,g10)
    c: InternalAlignment(g9,g10)
    c: InternalAlignment(g11,g10)
    c: InternalAlignment(g12,g10)
    c: Weight(g13) = 1
    c: Coincident(g16,g2)
    c: Equal(g13,g14)
    c: Equal(g13,g15)
    c: Coincident(g16,g3)
    c: InternalAlignment(g13,g16)
    c: InternalAlignment(g14,g16)
    c: InternalAlignment(g15,g16)
    c: InternalAlignment(g17,g16)
    c: InternalAlignment(g18,g16)
    c: Weight(g19) = 1
    c: Coincident(g22,g5)
    c: Equal(g19,g20)
    c: Equal(g19,g21)
    c: Coincident(g22,g6)
    c: InternalAlignment(g19,g22)
    c: InternalAlignment(g20,g22)
    c: InternalAlignment(g21,g22)
    c: InternalAlignment(g23,g22)
    c: InternalAlignment(g24,g22)
    c: Weight(g25) = 1
    c: Coincident(g28,g4)
    c: Equal(g25,g26)
    c: Equal(g25,g27)
    c: Coincident(g28,g3)
    c: InternalAlignment(g25,g28)
    c: InternalAlignment(g26,g28)
    c: InternalAlignment(g27,g28)
    c: InternalAlignment(g29,g28)
    c: InternalAlignment(g30,g28)
    c: Weight(g31) = 1
    c: Coincident(g34,g5)
    c: Equal(g31,g32)
    c: Equal(g31,g33)
    c: Coincident(g34,g6)
    c: InternalAlignment(g31,g34)
    c: InternalAlignment(g32,g34)
    c: InternalAlignment(g33,g34)
    c: InternalAlignment(g35,g34)
    c: InternalAlignment(g36,g34)
    c: Vertical(g37)
    c: Coincident(g37,g38)
    c: Horizontal(g38)
    c: Coincident(g38,g39)
    c: Vertical(g39)
    c: Coincident(g39,g40)
    c: Coincident(g40,g41)
    c: Vertical(g41)
    c: Coincident(g41,g42)
    c: Horizontal(g42)
    c: Coincident(g42,g43)
    c: Vertical(g43)
    c: Vertical(g44)
    c: Coincident(g44,g45)
    c: Horizontal(g45)
    c: Coincident(g45,g46)
    c: Vertical(g46)
    c: Coincident(g46,g47)
    c: Horizontal(g47)
    c: Coincident(g47,g48)
    c: Coincident(g48,g49)
    c: Vertical(g49)
    c: Coincident(g49,g50)
    c: Horizontal(g50)
    c: Coincident(g50,g51)
    c: Vertical(g51)
    c: Horizontal(g48)
    c: Weight(g52) = 1
    c: Coincident(g55,g37)
    c: Equal(g52,g53)
    c: Equal(g52,g54)
    c: Coincident(g55,g51)
    c: InternalAlignment(g52,g55)
    c: InternalAlignment(g53,g55)
    c: InternalAlignment(g54,g55)
    c: InternalAlignment(g56,g55)
    c: InternalAlignment(g57,g55)
    c: Weight(g58) = 1
    c: Coincident(g61,g43)
    c: Equal(g58,g59)
    c: Equal(g58,g60)
    c: Coincident(g61,g44)
    c: InternalAlignment(g58,g61)
    c: InternalAlignment(g59,g61)
    c: InternalAlignment(g60,g61)
    c: InternalAlignment(g62,g61)
    c: InternalAlignment(g63,g61)
FEATURE [PartDesign::Pocket] Pocket007
  BaseFeature = -> Pocket005
  Direction = (0,0,-1)
  Length = 2
  Length2 = 5
  Profile = -> Sketch030
  ReferenceAxis = -> Sketch030 [N_Axis]
  Type = 0
FEATURE [Sketcher::SketchObject] Sketch031
  FullyConstrained = false
  MapMode = 5
  Placement = pos=(0,69,0) rot=(0,0.707107,0.707107;3.14159rad)
  Support = -> [Pocket006]
  sketch-geometry (29):
    g0: LineSegment StartX=63.5263 StartY=98.4803 StartZ=0 EndX=66.5263 EndY=98.4803 EndZ=0
    g1: LineSegment StartX=66.5263 StartY=98.4803 StartZ=0 EndX=66.5263 EndY=68.4803 EndZ=0
    g2: LineSegment StartX=66.5263 StartY=68.4803 StartZ=0 EndX=63.5263 EndY=68.4803 EndZ=0
    g3: LineSegment StartX=63.5263 StartY=68.4803 StartZ=0 EndX=63.5263 EndY=98.4803 EndZ=0
    g4: LineSegment StartX=69.5263 StartY=98.4803 StartZ=0 EndX=72.5263 EndY=98.4803 EndZ=0
    g5: LineSegment StartX=72.5263 StartY=98.4803 StartZ=0 EndX=72.5263 EndY=68.4803 EndZ=0
    g6: LineSegment StartX=72.5263 StartY=68.4803 StartZ=0 EndX=69.5263 EndY=68.4803 EndZ=0
    g7: LineSegment StartX=69.5263 StartY=68.4803 StartZ=0 EndX=69.5263 EndY=98.4803 EndZ=0
    g8: LineSegment StartX=75.5263 StartY=98.4803 StartZ=0 EndX=78.5263 EndY=98.4803 EndZ=0
    g9: LineSegment StartX=78.5263 StartY=98.4803 StartZ=0 EndX=78.5263 EndY=68.4803 EndZ=0
    g10: LineSegment StartX=78.5263 StartY=68.4803 StartZ=0 EndX=75.5263 EndY=68.4803 EndZ=0
    g11: LineSegment StartX=75.5263 StartY=68.4803 StartZ=0 EndX=75.5263 EndY=98.4803 EndZ=0
    g12: LineSegment StartX=66.5263 StartY=98.4803 StartZ=0 EndX=69.5263 EndY=98.4803 EndZ=0
    g13: LineSegment StartX=72.5263 StartY=98.4803 StartZ=0 EndX=75.5263 EndY=98.4803 EndZ=0
    g14: LineSegment StartX=81.5263 StartY=98.4803 StartZ=0 EndX=84.5263 EndY=98.4803 EndZ=0
    g15: LineSegment StartX=84.5263 StartY=98.4803 StartZ=0 EndX=84.5263 EndY=68.4803 EndZ=0
    g16: LineSegment StartX=84.5263 StartY=68.4803 StartZ=0 EndX=81.5263 EndY=68.4803 EndZ=0
    g17: LineSegment StartX=81.5263 StartY=68.4803 StartZ=0 EndX=81.5263 EndY=98.4803 EndZ=0
    g18: LineSegment StartX=87.5263 StartY=98.4803 StartZ=0 EndX=90.5263 EndY=98.4803 EndZ=0
    g19: LineSegment StartX=90.5263 StartY=98.4803 StartZ=0 EndX=90.5263 EndY=68.4803 EndZ=0
    g20: LineSegment StartX=90.5263 StartY=68.4803 StartZ=0 EndX=87.5263 EndY=68.4803 EndZ=0
    g21: LineSegment StartX=87.5263 StartY=68.4803 StartZ=0 EndX=87.5263 EndY=98.4803 EndZ=0
    g22: LineSegment StartX=57.5263 StartY=98.4803 StartZ=0 EndX=60.5263 EndY=98.4803 EndZ=0
    g23: LineSegment StartX=60.5263 StartY=98.4803 StartZ=0 EndX=60.5263 EndY=68.057 EndZ=0
    g24: LineSegment StartX=60.5263 StartY=68.057 StartZ=0 EndX=57.5263 EndY=68.057 EndZ=0
    g25: LineSegment StartX=57.5263 StartY=68.057 StartZ=0 EndX=57.5263 EndY=98.4803 EndZ=0
    g26: LineSegment StartX=78.5263 StartY=98.4803 StartZ=0 EndX=81.5263 EndY=98.4803 EndZ=0
    g27: LineSegment StartX=84.5263 StartY=98.4803 StartZ=0 EndX=87.5263 EndY=98.4803 EndZ=0
    g28: LineSegment StartX=60.5263 StartY=98.4803 StartZ=0 EndX=63.5263 EndY=98.4803 EndZ=0
  constraints (79):
    c: Coincident(g0,g1)
    c: Coincident(g1,g2)
    c: Coincident(g2,g3)
    c: Coincident(g3,g0)
    c: Horizontal(g0)
    c: Horizontal(g2)
    c: Vertical(g1)
    c: Vertical(g3)
    c: Coincident(g4,g5)
    c: Coincident(g5,g6)
    c: Coincident(g6,g7)
    c: Coincident(g7,g4)
    c: Horizontal(g4)
    c: Horizontal(g6)
    c: Vertical(g5)
    c: Vertical(g7)
    c: Coincident(g8,g9)
    c: Coincident(g9,g10)
    c: Coincident(g10,g11)
    c: Coincident(g11,g8)
    c: Horizontal(g8)
    c: Horizontal(g10)
    c: Vertical(g9)
    c: Vertical(g11)
    c: DistanceX(g0,g0) = 3
    c: DistanceY(g3,g3) = 30
    c: Coincident(g12,g0)
    c: Coincident(g12,g4)
    c: Horizontal(g12)
    c: DistanceY(g7,g7) = 30
    c: DistanceX(g4,g4) = 3
    c: DistanceX(g12,g12) = 3
    c: DistanceY(g11,g11) = 30
    c: Coincident(g13,g4)
    c: Coincident(g13,g8)
    c: Horizontal(g13)
    c: DistanceX(g13,g13) = 3
    c: DistanceX(g8,g8) = 3
    c: Coincident(g14,g15)
    c: Coincident(g15,g16)
    c: Coincident(g16,g17)
    c: Coincident(g17,g14)
    c: Horizontal(g14)
    c: Horizontal(g16)
    c: Vertical(g15)
    c: Vertical(g17)
    c: Coincident(g18,g19)
    c: Coincident(g19,g20)
    c: Coincident(g20,g21)
    c: Coincident(g21,g18)
    c: Horizontal(g18)
    c: Horizontal(g20)
    c: Vertical(g19)
    c: Vertical(g21)
    c: Coincident(g22,g23)
    c: Coincident(g23,g24)
    c: Coincident(g24,g25)
    c: Coincident(g25,g22)
    c: Horizontal(g22)
    c: Horizontal(g24)
    c: Vertical(g23)
    c: Vertical(g25)
    c: DistanceY(g17,g17) = 30
    c: Coincident(g26,g8)
    c: Coincident(g26,g14)
    c: Horizontal(g26)
    c: DistanceX(g26,g26) = 3
    c: Coincident(g27,g14)
    c: Coincident(g27,g18)
    c: Horizontal(g27)
    c: DistanceX(g14,g14) = 3
    c: DistanceX(g27,g27) = 3
    c: DistanceX(g18,g18) = 3
    c: DistanceX(g22,g22) = 3
    c: DistanceY(g21,g21) = 30
    c: Coincident(g28,g22)
    c: Coincident(g28,g0)
    c: Horizontal(g28)
    c: DistanceX(g28,g28) = 3
FEATURE [PartDesign::Pocket] Pocket008
  BaseFeature = -> Pocket006
  Direction = (0,-1,2e-16)
  Length = 5
  Length2 = 5
  Profile = -> Sketch031
  ReferenceAxis = -> Sketch031 [N_Axis]
  Type = 0
FEATURE [Sketcher::SketchObject] Sketch032
  FullyConstrained = false
  MapMode = 5
  Placement = pos=(0,-69,0) rot=(1,0,0;1.5708rad)
  Support = -> [Pocket008]
  sketch-geometry (29):
    g0: LineSegment StartX=-60.5353 StartY=98.473 StartZ=0 EndX=-57.5353 EndY=98.473 EndZ=0
    g1: LineSegment StartX=-57.5353 StartY=98.473 StartZ=0 EndX=-57.5353 EndY=68.473 EndZ=0
    g2: LineSegment StartX=-57.5353 StartY=68.473 StartZ=0 EndX=-60.5353 EndY=68.473 EndZ=0
    g3: LineSegment StartX=-60.5353 StartY=68.473 StartZ=0 EndX=-60.5353 EndY=98.473 EndZ=0
    g4: LineSegment StartX=-90.5353 StartY=98.473 StartZ=0 EndX=-87.5353 EndY=98.473 EndZ=0
    g5: LineSegment StartX=-87.5353 StartY=98.473 StartZ=0 EndX=-87.5353 EndY=68.473 EndZ=0
    g6: LineSegment StartX=-87.5353 StartY=68.473 StartZ=0 EndX=-90.5353 EndY=68.473 EndZ=0
    g7: LineSegment StartX=-90.5353 StartY=68.473 StartZ=0 EndX=-90.5353 EndY=98.473 EndZ=0
    g8: LineSegment StartX=-84.5353 StartY=98.473 StartZ=0 EndX=-81.5353 EndY=98.473 EndZ=0
    g9: LineSegment StartX=-81.5353 StartY=98.473 StartZ=0 EndX=-81.5353 EndY=68.473 EndZ=0
    g10: LineSegment StartX=-81.5353 StartY=68.473 StartZ=0 EndX=-84.5353 EndY=68.473 EndZ=0
    g11: LineSegment StartX=-84.5353 StartY=68.473 StartZ=0 EndX=-84.5353 EndY=98.473 EndZ=0
    g12: LineSegment StartX=-78.5353 StartY=98.473 StartZ=0 EndX=-75.5353 EndY=98.473 EndZ=0
    g13: LineSegment StartX=-75.5353 StartY=98.473 StartZ=0 EndX=-75.5353 EndY=68.473 EndZ=0
    g14: LineSegment StartX=-75.5353 StartY=68.473 StartZ=0 EndX=-78.5353 EndY=68.473 EndZ=0
    g15: LineSegment StartX=-78.5353 StartY=68.473 StartZ=0 EndX=-78.5353 EndY=98.473 EndZ=0
    g16: LineSegment StartX=-72.5353 StartY=98.473 StartZ=0 EndX=-69.5353 EndY=98.473 EndZ=0
    g17: LineSegment StartX=-69.5353 StartY=98.473 StartZ=0 EndX=-69.5353 EndY=68.473 EndZ=0
    g18: LineSegment StartX=-69.5353 StartY=68.473 StartZ=0 EndX=-72.5353 EndY=68.473 EndZ=0
    g19: LineSegment StartX=-72.5353 StartY=68.473 StartZ=0 EndX=-72.5353 EndY=98.473 EndZ=0
    g20: LineSegment StartX=-66.5353 StartY=98.473 StartZ=0 EndX=-63.5353 EndY=98.473 EndZ=0
    g21: LineSegment StartX=-63.5353 StartY=98.473 StartZ=0 EndX=-63.5353 EndY=68.473 EndZ=0
    g22: LineSegment StartX=-63.5353 StartY=68.473 StartZ=0 EndX=-66.5353 EndY=68.473 EndZ=0
    g23: LineSegment StartX=-66.5353 StartY=68.473 StartZ=0 EndX=-66.5353 EndY=98.473 EndZ=0
    g24: LineSegment StartX=-87.5353 StartY=98.473 StartZ=0 EndX=-84.5353 EndY=98.473 EndZ=0
    g25: LineSegment StartX=-81.5353 StartY=98.473 StartZ=0 EndX=-78.5353 EndY=98.473 EndZ=0
    g26: LineSegment StartX=-75.5353 StartY=98.473 StartZ=0 EndX=-72.5353 EndY=98.473 EndZ=0
    g27: LineSegment StartX=-69.5353 StartY=98.473 StartZ=0 EndX=-66.5353 EndY=98.473 EndZ=0
    g28: LineSegment StartX=-63.5353 StartY=98.473 StartZ=0 EndX=-60.5353 EndY=98.473 EndZ=0
  constraints (80):
    c: Coincident(g0,g1)
    c: Coincident(g1,g2)
    c: Coincident(g2,g3)
    c: Coincident(g3,g0)
    c: Horizontal(g0)
    c: Horizontal(g2)
    c: Vertical(g1)
    c: Vertical(g3)
    c: Coincident(g4,g5)
    c: Coincident(g5,g6)
    c: Coincident(g6,g7)
    c: Coincident(g7,g4)
    c: Horizontal(g4)
    c: Horizontal(g6)
    c: Vertical(g5)
    c: Vertical(g7)
    c: Coincident(g8,g9)
    c: Coincident(g9,g10)
    c: Coincident(g10,g11)
    c: Coincident(g11,g8)
    c: Horizontal(g8)
    c: Horizontal(g10)
    c: Vertical(g9)
    c: Vertical(g11)
    c: Coincident(g12,g13)
    c: Coincident(g13,g14)
    c: Coincident(g14,g15)
    c: Coincident(g15,g12)
    c: Horizontal(g12)
    c: Horizontal(g14)
    c: Vertical(g13)
    c: Vertical(g15)
    c: Coincident(g16,g17)
    c: Coincident(g17,g18)
    c: Coincident(g18,g19)
    c: Coincident(g19,g16)
    c: Horizontal(g16)
    c: Horizontal(g18)
    c: Vertical(g17)
    c: Vertical(g19)
    c: Coincident(g20,g21)
    c: Coincident(g21,g22)
    c: Coincident(g22,g23)
    c: Coincident(g23,g20)
    c: Horizontal(g20)
    c: Horizontal(g22)
    c: Vertical(g21)
    c: Vertical(g23)
    c: DistanceX(g0,g0) = 3
    c: DistanceX(g4,g4) = 3
    c: DistanceX(g8,g8) = 3
    c: DistanceX(g12,g12) = 3
    c: DistanceX(g16,g16) = 3
    c: DistanceX(g20,g20) = 3
    c: Coincident(g24,g4)
    c: Coincident(g24,g8)
    c: Coincident(g25,g8)
    c: Coincident(g25,g12)
    c: Horizontal(g25)
    c: Coincident(g26,g12)
    c: Coincident(g26,g16)
    c: Horizontal(g26)
    c: Coincident(g27,g16)
    c: Coincident(g27,g20)
    c: Horizontal(g27)
    c: Horizontal(g24)
    c: DistanceY(g3,g3) = 30
    c: DistanceY(g7,g7) = 30
    c: DistanceY(g11,g11) = 30
    c: DistanceY(g15,g15) = 30
    c: DistanceY(g19,g19) = 30
    c: DistanceY(g23,g23) = 30
    c: DistanceX(g24,g24) = 3
    c: DistanceX(g25,g25) = 3
    c: DistanceX(g26,g26) = 3
    c: DistanceX(g27,g27) = 3
    c: Coincident(g28,g20)
    c: Coincident(g28,g0)
    c: Horizontal(g28)
    c: DistanceX(g28,g28) = 3
FEATURE [PartDesign::Pocket] Pocket009
  BaseFeature = -> Pocket008
  Direction = (0,1,-2e-16)
  Length = 5
  Length2 = 5
  Profile = -> Sketch032
  ReferenceAxis = -> Sketch032 [N_Axis]
  Type = 0
FEATURE [Sketcher::SketchObject] Sketch033
  FullyConstrained = false
  MapMode = 5
  Placement = pos=(129,0,0) rot=(0.57735,0.57735,0.57735;2.0944rad)
  Support = -> [Pocket009]
  sketch-geometry (161):
    g0: LineSegment StartX=-47.4972 StartY=73.486 StartZ=0 EndX=-47.4972 EndY=80.0254 EndZ=0
    g1: LineSegment StartX=-47.4972 StartY=80.0254 StartZ=0 EndX=-63.3882 EndY=80.0254 EndZ=0
    g2: LineSegment StartX=-63.3882 StartY=80.0254 StartZ=0 EndX=-63.3882 EndY=73.5191 EndZ=0
    g3: LineSegment StartX=-49.9628 StartY=70.9402 StartZ=0 EndX=-60.9677 EndY=70.9402 EndZ=0
    g4: Circle CenterX=-63.3882 CenterY=73.5191 CenterZ=0 NormalX=0 NormalY=0 NormalZ=1 AngleXU=0 Radius=1
    g5: Circle CenterX=-63.2031 CenterY=70.9984 CenterZ=0 NormalX=0 NormalY=0 NormalZ=1 AngleXU=0 Radius=1
    g6: Circle CenterX=-60.9677 CenterY=70.9402 CenterZ=0 NormalX=0 NormalY=0 NormalZ=1 AngleXU=0 Radius=1
    g7: BSplineCurve PolesCount=3 KnotsCount=2 Degree=2 IsPeriodic=0
    g8: GeomPoint X=-63.3882 Y=73.5191 Z=0
    g9: GeomPoint X=-60.9677 Y=70.9402 Z=0
    g10: Circle CenterX=-49.9628 CenterY=70.9402 CenterZ=0 NormalX=0 NormalY=0 NormalZ=1 AngleXU=0 Radius=1
    g11: Circle CenterX=-47.9022 CenterY=71.4182 CenterZ=0 NormalX=0 NormalY=0 NormalZ=1 AngleXU=0 Radius=1
    g12: Circle CenterX=-47.4972 CenterY=73.486 CenterZ=0 NormalX=0 NormalY=0 NormalZ=1 AngleXU=0 Radius=1
    g13: BSplineCurve PolesCount=3 KnotsCount=2 Degree=2 IsPeriodic=0
    g14: GeomPoint X=-49.9628 Y=70.9402 Z=0
    g15: GeomPoint X=-47.4972 Y=73.486 Z=0
    g16: LineSegment StartX=-49.0197 StartY=77.9908 StartZ=0 EndX=-61.8584 EndY=77.9908 EndZ=0
    g17: LineSegment StartX=-61.8584 StartY=77.9908 StartZ=0 EndX=-61.8584 EndY=74.6599 EndZ=0
    g18: LineSegment StartX=-60.3584 StartY=73.1599 StartZ=0 EndX=-50.5197 EndY=73.1599 EndZ=0
    g19: LineSegment StartX=-49.0197 StartY=74.6599 StartZ=0 EndX=-49.0197 EndY=77.9908 EndZ=0
    g20: ArcOfCircle CenterX=-60.3584 CenterY=74.6599 CenterZ=0 NormalX=0 NormalY=0 NormalZ=1 AngleXU=0 Radius=1.5 StartAngle=3.14159 EndAngle=4.71239
    g21: ArcOfCircle CenterX=-50.5197 CenterY=74.6599 CenterZ=0 NormalX=0 NormalY=0 NormalZ=1 AngleXU=0 Radius=1.5 StartAngle=4.71239 EndAngle=6.28319
    g22: LineSegment StartX=-63.4208 StartY=70.1973 StartZ=0 EndX=-48.0618 EndY=70.1973 EndZ=0
    g23: LineSegment StartX=-47.6102 StartY=69.7458 StartZ=0 EndX=-47.6102 EndY=68.3212 EndZ=0
    g24: LineSegment StartX=-48.0305 StartY=67.9009 StartZ=0 EndX=-63.4208 EndY=67.9009 EndZ=0
    g25: LineSegment StartX=-63.4208 StartY=67.9009 StartZ=0 EndX=-63.4208 EndY=70.1973 EndZ=0
    g26: ArcOfCircle CenterX=-48.0305 CenterY=68.3212 CenterZ=0 NormalX=0 NormalY=0 NormalZ=1 AngleXU=0 Radius=0.420335 StartAngle=4.71239 EndAngle=6.28319
    g27: ArcOfCircle CenterX=-48.0618 CenterY=69.7458 CenterZ=0 NormalX=0 NormalY=0 NormalZ=1 AngleXU=0 Radius=0.45159 StartAngle=-9e-16 EndAngle=1.5708
    g28: LineSegment StartX=-47.611 StartY=64.3295 StartZ=0 EndX=-47.611 EndY=60.4029 EndZ=0
    g29: LineSegment StartX=-49.673 StartY=63.9959 StartZ=0 EndX=-49.673 EndY=61.3146 EndZ=0
    g30: Circle CenterX=-47.611 CenterY=60.4029 CenterZ=0 NormalX=0 NormalY=0 NormalZ=1 AngleXU=0 Radius=1
    g31: Circle CenterX=-48.2314 CenterY=58.8127 CenterZ=0 NormalX=0 NormalY=0 NormalZ=1 AngleXU=0 Radius=1
    g32: Circle CenterX=-49.9984 CenterY=58.4006 CenterZ=0 NormalX=0 NormalY=0 NormalZ=1 AngleXU=0 Radius=1
    g33: BSplineCurve PolesCount=3 KnotsCount=2 Degree=2 IsPeriodic=0
    g34: GeomPoint X=-47.611 Y=60.4029 Z=0
    g35: GeomPoint X=-49.9984 Y=58.4006 Z=0
    g36: LineSegment StartX=-49.9984 StartY=58.4006 StartZ=0 EndX=-51.5155 EndY=58.4006 EndZ=0
    g37: LineSegment StartX=-51.5155 StartY=60.6899 StartZ=0 EndX=-50.5162 EndY=60.6899 EndZ=0
    g38: Circle CenterX=-49.673 CenterY=61.3146 CenterZ=0 NormalX=0 NormalY=0 NormalZ=1 AngleXU=0 Radius=1
    g39: Circle CenterX=-49.7306 CenterY=60.6866 CenterZ=0 NormalX=0 NormalY=0 NormalZ=1 AngleXU=0 Radius=1
    g40: Circle CenterX=-50.5162 CenterY=60.6899 CenterZ=0 NormalX=0 NormalY=0 NormalZ=1 AngleXU=0 Radius=1
    g41: BSplineCurve PolesCount=3 KnotsCount=2 Degree=2 IsPeriodic=0
    g42: GeomPoint X=-49.673 Y=61.3146 Z=0
    g43: GeomPoint X=-50.5162 Y=60.6899 Z=0
    g44: Circle CenterX=-47.611 CenterY=64.3295 CenterZ=0 NormalX=0 NormalY=0 NormalZ=1 AngleXU=0 Radius=1
    g45: Circle CenterX=-47.9312 CenterY=66.4658 CenterZ=0 NormalX=0 NormalY=0 NormalZ=1 AngleXU=0 Radius=1
    g46: Circle CenterX=-49.9147 CenterY=67.0474 CenterZ=0 NormalX=0 NormalY=0 NormalZ=1 AngleXU=0 Radius=1
    g47: BSplineCurve PolesCount=3 KnotsCount=2 Degree=2 IsPeriodic=0
    g48: GeomPoint X=-47.611 Y=64.3295 Z=0
    g49: GeomPoint X=-49.9147 Y=67.0474 Z=0
    g50: LineSegment StartX=-49.9147 StartY=67.0474 StartZ=0 EndX=-61.0707 EndY=67.0474 EndZ=0
    g51: Circle CenterX=-61.0707 CenterY=67.0474 CenterZ=0 NormalX=0 NormalY=0 NormalZ=1 AngleXU=0 Radius=1
    g52: Circle CenterX=-63.1953 CenterY=66.6956 CenterZ=0 NormalX=0 NormalY=0 NormalZ=1 AngleXU=0 Radius=1
    g53: Circle CenterX=-63.6371 CenterY=64.2279 CenterZ=0 NormalX=0 NormalY=0 NormalZ=1 AngleXU=0 Radius=1
    g54: BSplineCurve PolesCount=3 KnotsCount=2 Degree=2 IsPeriodic=0
    g55: GeomPoint X=-61.0707 Y=67.0474 Z=0
    g56: GeomPoint X=-63.6371 Y=64.2279 Z=0
    g57: LineSegment StartX=-63.6371 StartY=64.2279 StartZ=0 EndX=-63.6371 EndY=60.7883 EndZ=0
    g58: LineSegment StartX=-61.4899 StartY=58.4268 StartZ=0 EndX=-60.0364 EndY=58.4268 EndZ=0
    g59: LineSegment StartX=-60.0364 StartY=58.4268 StartZ=0 EndX=-60.0364 EndY=60.6979 EndZ=0
    g60: LineSegment StartX=-60.0364 StartY=60.6979 StartZ=0 EndX=-61.0085 EndY=60.6979 EndZ=0
    g61-g64: Circle x4 (B-spline internal-alignment scaffolding for g65; pole/knot coordinates omitted)
    g65: BSplineCurve PolesCount=4 KnotsCount=2 Degree=3 IsPeriodic=0
    g66: GeomPoint X=-63.6371 Y=60.7883 Z=0
    g67: GeomPoint X=-61.4899 Y=58.4268 Z=0
    g68: LineSegment StartX=-61.7338 StartY=64.169 StartZ=0 EndX=-61.7338 EndY=61.2157 EndZ=0
    g69: Circle CenterX=-61.7338 CenterY=61.2157 CenterZ=0 NormalX=0 NormalY=0 NormalZ=1 AngleXU=0 Radius=1
    g70: Circle CenterX=-61.7159 CenterY=60.6636 CenterZ=0 NormalX=0 NormalY=0 NormalZ=1 AngleXU=0 Radius=1
    g71: Circle CenterX=-61.0085 CenterY=60.6979 CenterZ=0 NormalX=0 NormalY=0 NormalZ=1 AngleXU=0 Radius=1
    g72: BSplineCurve PolesCount=3 KnotsCount=2 Degree=2 IsPeriodic=0
    g73: GeomPoint X=-61.7338 Y=61.2157 Z=0
    g74: GeomPoint X=-61.0085 Y=60.6979 Z=0
    g75: LineSegment StartX=-61.1833 StartY=64.7357 StartZ=0 EndX=-50.7106 EndY=64.7357 EndZ=0
    g76-g79: Circle x4 (B-spline internal-alignment scaffolding for g80; pole/knot coordinates omitted)
    g80: BSplineCurve PolesCount=4 KnotsCount=2 Degree=3 IsPeriodic=0
    g81: GeomPoint X=-49.673 Y=63.9959 Z=0
    g82: GeomPoint X=-50.7106 Y=64.7357 Z=0
    g83-g86: Circle x4 (B-spline internal-alignment scaffolding for g87; pole/knot coordinates omitted)
    g87: BSplineCurve PolesCount=4 KnotsCount=2 Degree=3 IsPeriodic=0
    g88: GeomPoint X=-61.1833 Y=64.7357 Z=0
    g89: GeomPoint X=-61.7338 Y=64.169 Z=0
    g90: LineSegment StartX=-51.5155 StartY=60.6899 StartZ=0 EndX=-51.5155 EndY=58.4006 EndZ=0
    g91: LineSegment StartX=-47.5898 StartY=50.6745 StartZ=0 EndX=-47.5898 EndY=57.4268 EndZ=0
    g92: LineSegment StartX=-47.5898 StartY=57.4268 StartZ=0 EndX=-63.4252 EndY=57.4268 EndZ=0
    g93: LineSegment StartX=-63.4252 StartY=57.4268 StartZ=0 EndX=-63.4252 EndY=50.5808 EndZ=0
    g94: Circle CenterX=-47.5898 CenterY=50.6745 CenterZ=0 NormalX=0 NormalY=0 NormalZ=1 AngleXU=0 Radius=1
    g95: Circle CenterX=-48.0508 CenterY=48.846 CenterZ=0 NormalX=0 NormalY=0 NormalZ=1 AngleXU=0 Radius=1
    g96: Circle CenterX=-49.9242 CenterY=48.6762 CenterZ=0 NormalX=0 NormalY=0 NormalZ=1 AngleXU=0 Radius=1
    g97: BSplineCurve PolesCount=3 KnotsCount=2 Degree=2 IsPeriodic=0
    g98: GeomPoint X=-47.5898 Y=50.6745 Z=0
    g99: GeomPoint X=-49.9242 Y=48.6762 Z=0
    g100: LineSegment StartX=-49.9242 StartY=48.6762 StartZ=0 EndX=-54.057 EndY=48.6762 EndZ=0
    g101-g104: Circle x4 (B-spline internal-alignment scaffolding for g105; pole/knot coordinates omitted)
    g105: BSplineCurve PolesCount=4 KnotsCount=2 Degree=3 IsPeriodic=0
    g106: GeomPoint X=-54.057 Y=48.6762 Z=0
    g107: GeomPoint X=-55.1673 Y=49.6274 Z=0
    g108-g111: Circle x4 (B-spline internal-alignment scaffolding for g112; pole/knot coordinates omitted)
    g112: BSplineCurve PolesCount=4 KnotsCount=2 Degree=3 IsPeriodic=0
    g113: GeomPoint X=-55.1673 Y=49.6274 Z=0
    g114: GeomPoint X=-56.4986 Y=48.3244 Z=0
    g115: LineSegment StartX=-56.4986 StartY=48.3244 StartZ=0 EndX=-61.5544 EndY=48.3244 EndZ=0
    g116-g119: Circle x4 (B-spline internal-alignment scaffolding for g120; pole/knot coordinates omitted)
    g120: BSplineCurve PolesCount=4 KnotsCount=2 Degree=3 IsPeriodic=0
    g121: GeomPoint X=-61.5544 Y=48.3244 Z=0
    g122: GeomPoint X=-63.4252 Y=50.5808 Z=0
    g123: LineSegment StartX=-56.1522 StartY=55.332 StartZ=0 EndX=-61.6559 EndY=55.332 EndZ=0
    g124: LineSegment StartX=-61.6559 StartY=55.332 StartZ=0 EndX=-61.6559 EndY=51.3317 EndZ=0
    g125: LineSegment StartX=-60.6818 StartY=50.3576 StartZ=0 EndX=-57.0088 EndY=50.3576 EndZ=0
    g126: LineSegment StartX=-56.1522 StartY=51.2141 StartZ=0 EndX=-56.1522 EndY=55.332 EndZ=0
    g127: ArcOfCircle CenterX=-57.0088 CenterY=51.2141 CenterZ=0 NormalX=0 NormalY=0 NormalZ=1 AngleXU=0 Radius=0.856579 StartAngle=4.71239 EndAngle=6.28319
    g128: ArcOfCircle CenterX=-60.6818 CenterY=51.3317 CenterZ=0 NormalX=0 NormalY=0 NormalZ=1 AngleXU=0 Radius=0.97414 StartAngle=3.14159 EndAngle=4.71239
    g129: LineSegment StartX=-49.5042 StartY=55.2608 StartZ=0 EndX=-54.4643 EndY=55.2608 EndZ=0
    g130: LineSegment StartX=-54.4643 StartY=55.2608 StartZ=0 EndX=-54.4643 EndY=51.6158 EndZ=0
    g131: LineSegment StartX=-53.7319 StartY=50.8835 StartZ=0 EndX=-50.2116 EndY=50.8835 EndZ=0
    g132: LineSegment StartX=-49.5042 StartY=51.5909 StartZ=0 EndX=-49.5042 EndY=55.2608 EndZ=0
    g133: ArcOfCircle CenterX=-50.2116 CenterY=51.5909 CenterZ=0 NormalX=0 NormalY=0 NormalZ=1 AngleXU=0 Radius=0.707444 StartAngle=4.71239 EndAngle=6.28319
    g134: ArcOfCircle CenterX=-53.7319 CenterY=51.6158 CenterZ=0 NormalX=0 NormalY=0 NormalZ=1 AngleXU=0 Radius=0.732321 StartAngle=3.14159 EndAngle=4.71239
    g135: LineSegment StartX=-50.543 StartY=45.2581 StartZ=0 EndX=-60.3966 EndY=45.2581 EndZ=0
    g136: LineSegment StartX=-61.4609 StartY=44.1939 StartZ=0 EndX=-61.4609 EndY=41.6882 EndZ=0
    g137: LineSegment StartX=-60.3966 StartY=40.6239 StartZ=0 EndX=-50.543 EndY=40.6239 EndZ=0
    g138: LineSegment StartX=-49.4787 StartY=41.6882 StartZ=0 EndX=-49.4787 EndY=44.1939 EndZ=0
    g139: ArcOfCircle CenterX=-50.543 CenterY=44.1939 CenterZ=0 NormalX=0 NormalY=0 NormalZ=1 AngleXU=0 Radius=1.06425 StartAngle=-9e-16 EndAngle=1.5708
    g140: ArcOfCircle CenterX=-50.543 CenterY=41.6882 CenterZ=0 NormalX=0 NormalY=0 NormalZ=1 AngleXU=0 Radius=1.06425 StartAngle=4.71239 EndAngle=6.28319
    g141: ArcOfCircle CenterX=-60.3966 CenterY=41.6882 CenterZ=0 NormalX=0 NormalY=0 NormalZ=1 AngleXU=0 Radius=1.06425 StartAngle=3.14159 EndAngle=4.71239
    g142: ArcOfCircle CenterX=-60.3966 CenterY=44.1939 CenterZ=0 NormalX=0 NormalY=0 NormalZ=1 AngleXU=0 Radius=1.06425 StartAngle=1.5708 EndAngle=3.14159
    g143: LineSegment StartX=-49.5203 StartY=47.4707 StartZ=0 EndX=-61.2401 EndY=47.4707 EndZ=0
    g144: LineSegment StartX=-63.3807 StartY=45.3301 StartZ=0 EndX=-63.3807 EndY=40.5241 EndZ=0
    g145: LineSegment StartX=-61.2401 StartY=38.3835 StartZ=0 EndX=-49.5203 EndY=38.3835 EndZ=0
    g146: LineSegment StartX=-47.3798 StartY=40.5241 StartZ=0 EndX=-47.3798 EndY=45.3301 EndZ=0
    g147: ArcOfCircle CenterX=-49.5203 CenterY=45.3301 CenterZ=0 NormalX=0 NormalY=0 NormalZ=1 AngleXU=0 Radius=2.14058 StartAngle=1e-16 EndAngle=1.5708
    g148: ArcOfCircle CenterX=-49.5203 CenterY=40.5241 CenterZ=0 NormalX=0 NormalY=0 NormalZ=1 AngleXU=0 Radius=2.14058 StartAngle=4.71239 EndAngle=6.28319
    g149: ArcOfCircle CenterX=-61.2401 CenterY=40.5241 CenterZ=0 NormalX=0 NormalY=0 NormalZ=1 AngleXU=0 Radius=2.14058 StartAngle=3.14159 EndAngle=4.71239
    g150: ArcOfCircle CenterX=-61.2401 CenterY=45.3301 CenterZ=0 NormalX=0 NormalY=0 NormalZ=1 AngleXU=0 Radius=2.14058 StartAngle=1.5708 EndAngle=3.14159
    g151: LineSegment StartX=-49.9952 StartY=37.7803 StartZ=0 EndX=-48.4694 EndY=37.7803 EndZ=0
    g152: LineSegment StartX=-47.882 StartY=37.193 StartZ=0 EndX=-47.882 EndY=28.6233 EndZ=0
    g153: LineSegment StartX=-48.4134 StartY=28.092 StartZ=0 EndX=-50.056 EndY=28.092 EndZ=0
    g154: LineSegment StartX=-50.056 StartY=28.092 StartZ=0 EndX=-50.056 EndY=31.7951 EndZ=0
    g155: LineSegment StartX=-50.056 StartY=31.7951 StartZ=0 EndX=-63.7993 EndY=31.7951 EndZ=0
    g156: LineSegment StartX=-63.7993 StartY=31.7951 StartZ=0 EndX=-63.7993 EndY=34.1475 EndZ=0
    g157: LineSegment StartX=-63.7993 StartY=34.1475 StartZ=0 EndX=-49.9952 EndY=34.1475 EndZ=0
    g158: LineSegment StartX=-49.9952 StartY=34.1475 StartZ=0 EndX=-49.9952 EndY=37.7803 EndZ=0
    g159: ArcOfCircle CenterX=-48.4694 CenterY=37.193 CenterZ=0 NormalX=0 NormalY=0 NormalZ=1 AngleXU=0 Radius=0.587336 StartAngle=-9e-16 EndAngle=1.5708
    g160: ArcOfCircle CenterX=-48.4134 CenterY=28.6233 CenterZ=0 NormalX=0 NormalY=0 NormalZ=1 AngleXU=0 Radius=0.531354 StartAngle=4.71239 EndAngle=6.28319
  constraints (252):
    c: Vertical(g0)
    c: Coincident(g0,g1)
    c: Horizontal(g1)
    c: Coincident(g1,g2)
    c: Vertical(g2)
    c: Horizontal(g3)
    c: Weight(g4) = 1
    c: Coincident(g7,g2)
    c: Equal(g4,g5)
    c: Equal(g4,g6)
    c: Coincident(g7,g3)
    c: InternalAlignment(g4,g7)
    c: InternalAlignment(g5,g7)
    c: InternalAlignment(g6,g7)
    c: InternalAlignment(g8,g7)
    c: InternalAlignment(g9,g7)
    c: Weight(g10) = 1
    c: Coincident(g13,g3)
    c: Equal(g10,g11)
    c: Equal(g10,g12)
    c: Coincident(g13,g0)
    c: InternalAlignment(g10,g13)
    c: InternalAlignment(g11,g13)
    c: InternalAlignment(g12,g13)
    c: InternalAlignment(g14,g13)
    c: InternalAlignment(g15,g13)
    c: Coincident(g16,g17)
    c: Coincident(g19,g16)
    c: Horizontal(g16)
    c: Horizontal(g18)
    c: Vertical(g17)
    c: Vertical(g19)
    c: Tangent(g18,g20) = -1.5708
    c: Tangent(g17,g20) = -1.5708
    c: Tangent(g18,g21) = -1.5708
    c: Radius(g21) = 1.5
    c: Radius(g20) = 1.5
    c: Equal(g19,g17)
    c: Coincident(g24,g25)
    c: Coincident(g25,g22)
    c: Horizontal(g22)
    c: Horizontal(g24)
    c: Vertical(g23)
    c: Vertical(g25)
    c: Tangent(g23,g26) = 1.5708
    c: Tangent(g24,g26) = 1.5708
    c: Tangent(g23,g27) = 1.5708
    c: Tangent(g22,g27) = 1.5708
    c: Vertical(g28)
    c: Vertical(g29)
    c: Weight(g30) = 1
    c: Coincident(g33,g28)
    c: Equal(g30,g31)
    c: Equal(g30,g32)
    c: InternalAlignment(g30,g33)
    c: InternalAlignment(g31,g33)
    c: InternalAlignment(g32,g33)
    c: InternalAlignment(g34,g33)
    c: InternalAlignment(g35,g33)
    c: Coincident(g36,g33)
    c: Horizontal(g36)
    c: Horizontal(g37)
    c: Weight(g38) = 1
    c: Coincident(g41,g29)
    c: Equal(g38,g39)
    c: Equal(g38,g40)
    c: Coincident(g41,g37)
    c: InternalAlignment(g38,g41)
    c: InternalAlignment(g39,g41)
    c: InternalAlignment(g40,g41)
    c: InternalAlignment(g42,g41)
    c: InternalAlignment(g43,g41)
    c: Weight(g44) = 1
    c: Coincident(g47,g28)
    c: Equal(g44,g45)
    c: Equal(g44,g46)
    c: InternalAlignment(g44,g47)
    c: InternalAlignment(g45,g47)
    c: InternalAlignment(g46,g47)
    c: InternalAlignment(g48,g47)
    c: InternalAlignment(g49,g47)
    c: Coincident(g50,g47)
    c: Horizontal(g50)
    c: Weight(g51) = 1
    c: Coincident(g54,g50)
    c: Equal(g51,g52)
    c: Equal(g51,g53)
    c: InternalAlignment(g51,g54)
    c: InternalAlignment(g52,g54)
    c: InternalAlignment(g53,g54)
    c: InternalAlignment(g55,g54)
    c: InternalAlignment(g56,g54)
    c: Coincident(g57,g54)
    c: Vertical(g57)
    c: Horizontal(g58)
    c: Coincident(g58,g59)
    c: Coincident(g59,g60)
    c: Horizontal(g60)
    c: Weight(g61) = 1
    c: Coincident(g65,g57)
    c: Equal(g61,g62)
    c: Equal(g61,g63)
    c: Equal(g61,g64)
    c: Coincident(g65,g58)
    c: InternalAlignment(g61-g64 -> g65) x4
    c: InternalAlignment(g66,g65)
    c: InternalAlignment(g67,g65)
    c: Vertical(g59)
    c: Vertical(g68)
    c: Weight(g69) = 1
    c: Coincident(g72,g68)
    c: Equal(g69,g70)
    c: Equal(g69,g71)
    c: Coincident(g72,g60)
    c: InternalAlignment(g69,g72)
    c: InternalAlignment(g70,g72)
    c: InternalAlignment(g71,g72)
    c: InternalAlignment(g73,g72)
    c: InternalAlignment(g74,g72)
    c: Horizontal(g75)
    c: Weight(g76) = 1
    c: Coincident(g80,g29)
    c: Equal(g76,g77)
    c: Equal(g76,g78)
    c: Equal(g76,g79)
    c: Coincident(g80,g75)
    c: InternalAlignment(g76-g79 -> g80) x4
    c: InternalAlignment(g81,g80)
    c: InternalAlignment(g82,g80)
    c: Weight(g83) = 1
    c: Coincident(g87,g75)
    c: Equal(g83,g84)
    c: Equal(g83,g85)
    c: Equal(g83,g86)
    c: Coincident(g87,g68)
    c: InternalAlignment(g83-g86 -> g87) x4
    c: InternalAlignment(g88,g87)
    c: InternalAlignment(g89,g87)
    c: Coincident(g90,g37)
    c: Coincident(g90,g36)
    c: Vertical(g90)
    c: Vertical(g91)
    c: Coincident(g91,g92)
    c: Horizontal(g92)
    c: Tangent(g92,g64)
    c: Coincident(g92,g93)
    c: Vertical(g93)
    c: Weight(g94) = 1
    c: Equal(g94,g95)
    c: Equal(g94,g96)
    c: InternalAlignment(g94,g97)
    c: InternalAlignment(g95,g97)
    c: InternalAlignment(g96,g97)
    c: InternalAlignment(g98,g97)
    c: InternalAlignment(g99,g97)
    c: Coincident(g100,g97)
    c: Horizontal(g100)
    c: Weight(g101) = 1
    c: Coincident(g105,g100)
    c: Equal(g101,g102)
    c: Equal(g101,g103)
    c: Equal(g101,g104)
    c: InternalAlignment(g101-g104 -> g105) x4
    c: InternalAlignment(g106,g105)
    c: InternalAlignment(g107,g105)
    c: Weight(g108) = 1
    c: Coincident(g112,g105)
    c: Equal(g108,g109)
    c: Equal(g108,g110)
    c: Equal(g108,g111)
    c: InternalAlignment(g108-g111 -> g112) x4
    c: InternalAlignment(g113,g112)
    c: InternalAlignment(g114,g112)
    c: Coincident(g115,g112)
    c: Horizontal(g115)
    c: Weight(g116) = 1
    c: Coincident(g120,g115)
    c: Equal(g116,g117)
    c: Equal(g116,g118)
    c: Equal(g116,g119)
    c: Coincident(g120,g93)
    c: InternalAlignment(g116-g119 -> g120) x4
    c: InternalAlignment(g121,g120)
    c: InternalAlignment(g122,g120)
    c: Coincident(g123,g124)
    c: Coincident(g126,g123)
    c: Horizontal(g123)
    c: Horizontal(g125)
    c: Vertical(g124)
    c: Vertical(g126)
    c: Tangent(g126,g127) = -1.5708
    c: Tangent(g125,g127) = -1.5708
    c: Tangent(g125,g128) = -1.5708
    c: Tangent(g124,g128) = -1.5708
    c: Coincident(g129,g130)
    c: Coincident(g132,g129)
    c: Horizontal(g129)
    c: Horizontal(g131)
    c: Vertical(g130)
    c: Vertical(g132)
    c: Tangent(g132,g133) = -1.5708
    c: Tangent(g131,g133) = -1.5708
    c: Tangent(g131,g134) = -1.5708
    c: Tangent(g130,g134) = -1.5708
    c: Horizontal(g135)
    c: Horizontal(g137)
    c: Vertical(g136)
    c: Vertical(g138)
    c: Tangent(g138,g139) = -1.5708
    c: Tangent(g135,g139) = -1.5708
    c: Tangent(g138,g140) = -1.5708
    c: Tangent(g137,g140) = -1.5708
    c: Tangent(g136,g141) = -1.5708
    c: Tangent(g137,g141) = -1.5708
    c: Tangent(g136,g142) = -1.5708
    c: Tangent(g135,g142) = -1.5708
    c: Equal(g139,g140)
    c: Equal(g140,g141)
    c: Equal(g141,g142)
    c: Horizontal(g143)
    c: Horizontal(g145)
    c: Vertical(g144)
    c: Vertical(g146)
    c: Tangent(g146,g147) = -1.5708
    c: Tangent(g143,g147) = -1.5708
    c: Tangent(g146,g148) = -1.5708
    c: Tangent(g145,g148) = -1.5708
    c: Tangent(g144,g149) = -1.5708
    c: Tangent(g145,g149) = -1.5708
    c: Tangent(g144,g150) = -1.5708
    c: Tangent(g143,g150) = -1.5708
    c: Equal(g149,g150)
    c: Equal(g150,g148)
    c: Equal(g148,g147)
    c: Horizontal(g151)
    c: Vertical(g152)
    c: Horizontal(g153)
    c: Coincident(g153,g154)
    c: Vertical(g154)
    c: Coincident(g154,g155)
    c: Horizontal(g155)
    c: Coincident(g155,g156)
    c: Vertical(g156)
    c: Coincident(g156,g157)
    c: Horizontal(g157)
    c: Coincident(g157,g158)
    c: Coincident(g158,g151)
    c: Vertical(g158)
    c: Tangent(g152,g159) = 1.5708
    c: Tangent(g151,g159) = 1.5708
    c: Tangent(g152,g160) = 1.5708
    c: Tangent(g153,g160) = 1.5708
FEATURE [PartDesign::Pocket] Pocket010
  BaseFeature = -> Pocket009
  Direction = (-1,0,0)
  Length = 2
  Length2 = 5
  Profile = -> Sketch033
  ReferenceAxis = -> Sketch033 [N_Axis]
  Type = 0
FEATURE [Sketcher::SketchObject] Sketch034
  FullyConstrained = false
  MapMode = 5
  Placement = pos=(-129,0,0) rot=(0.57735,-0.57735,-0.57735;2.0944rad)
  Support = -> [Pocket010]
  sketch-geometry (129):
    g0: LineSegment StartX=47.9992 StartY=36.182 StartZ=0 EndX=47.9992 EndY=31.7484 EndZ=0
    g1: LineSegment StartX=50.3216 StartY=29.3959 StartZ=0 EndX=61.7827 EndY=29.3959 EndZ=0
    g2: LineSegment StartX=50.8344 StartY=31.6579 StartZ=0 EndX=61.3303 EndY=31.6579 EndZ=0
    g3: LineSegment StartX=51.7417 StartY=35.7296 StartZ=0 EndX=51.7417 EndY=37.9881 EndZ=0
    g4: LineSegment StartX=51.7417 StartY=37.9881 StartZ=0 EndX=49.8114 EndY=37.9881 EndZ=0
    g5: LineSegment StartX=51.7417 StartY=35.7296 StartZ=0 EndX=50.7439 EndY=35.7296 EndZ=0
    g6: LineSegment StartX=61.9939 StartY=32.3818 StartZ=0 EndX=61.9939 EndY=35.3074 EndZ=0
    g7: LineSegment StartX=60.3884 StartY=35.863 StartZ=0 EndX=60.3884 EndY=38.0044 EndZ=0
    g8: LineSegment StartX=60.3884 StartY=38.0044 StartZ=0 EndX=61.8732 EndY=37.9917 EndZ=0
    g9: LineSegment StartX=63.9845 StartY=32.1707 StartZ=0 EndX=63.9845 EndY=36.0312 EndZ=0
    g10: LineSegment StartX=50.0559 StartY=32.3029 StartZ=0 EndX=50.0559 EndY=35.2573 EndZ=0
    g11: Circle CenterX=47.9992 CenterY=36.182 CenterZ=0 NormalX=0 NormalY=0 NormalZ=1 AngleXU=0 Radius=1
    g12: BSplineCurve PolesCount=3 KnotsCount=2 Degree=2 IsPeriodic=0
    g13: GeomPoint X=49.8114 Y=37.9881 Z=0
    g14: GeomPoint X=47.9992 Y=36.182 Z=0
    g15-g18: Circle x4 (B-spline internal-alignment scaffolding for g19; pole/knot coordinates omitted)
    g19: BSplineCurve PolesCount=4 KnotsCount=2 Degree=3 IsPeriodic=0
    g20: GeomPoint X=50.3216 Y=29.3959 Z=0
    g21: GeomPoint X=47.9992 Y=31.7484 Z=0
    g22: Circle CenterX=50.8344 CenterY=31.6579 CenterZ=0 NormalX=0 NormalY=0 NormalZ=1 AngleXU=0 Radius=1
    g23: Circle CenterX=50.0353 CenterY=31.6188 CenterZ=0 NormalX=0 NormalY=0 NormalZ=1 AngleXU=0 Radius=1
    g24: Circle CenterX=50.0559 CenterY=32.3029 CenterZ=0 NormalX=0 NormalY=0 NormalZ=1 AngleXU=0 Radius=1
    g25: BSplineCurve PolesCount=3 KnotsCount=2 Degree=2 IsPeriodic=0
    g26: GeomPoint X=50.8344 Y=31.6579 Z=0
    g27: GeomPoint X=50.0559 Y=32.3029 Z=0
    g28: Circle CenterX=50.0559 CenterY=35.2573 CenterZ=0 NormalX=0 NormalY=0 NormalZ=1 AngleXU=0 Radius=1
    g29: Circle CenterX=50.1021 CenterY=35.7695 CenterZ=0 NormalX=0 NormalY=0 NormalZ=1 AngleXU=0 Radius=1
    g30: Circle CenterX=50.7439 CenterY=35.7296 CenterZ=0 NormalX=0 NormalY=0 NormalZ=1 AngleXU=0 Radius=1
    g31: BSplineCurve PolesCount=3 KnotsCount=2 Degree=2 IsPeriodic=0
    g32: GeomPoint X=50.0559 Y=35.2573 Z=0
    g33: GeomPoint X=50.7439 Y=35.7296 Z=0
    g34: Circle CenterX=61.7827 CenterY=29.3959 CenterZ=0 NormalX=0 NormalY=0 NormalZ=1 AngleXU=0 Radius=1
    g35: Circle CenterX=63.9854 CenterY=29.698 CenterZ=0 NormalX=0 NormalY=0 NormalZ=1 AngleXU=0 Radius=1
    g36: Circle CenterX=63.9845 CenterY=32.1707 CenterZ=0 NormalX=0 NormalY=0 NormalZ=1 AngleXU=0 Radius=1
    g37: BSplineCurve PolesCount=3 KnotsCount=2 Degree=2 IsPeriodic=0
    g38: GeomPoint X=61.7827 Y=29.3959 Z=0
    g39: GeomPoint X=63.9845 Y=32.1707 Z=0
    g40: Circle CenterX=63.9845 CenterY=36.0312 CenterZ=0 NormalX=0 NormalY=0 NormalZ=1 AngleXU=0 Radius=1
    g41: BSplineCurve PolesCount=3 KnotsCount=2 Degree=2 IsPeriodic=0
    g42: GeomPoint X=63.9845 Y=36.0312 Z=0
    g43: GeomPoint X=61.8732 Y=37.9917 Z=0
    g44: Circle CenterX=61.9939 CenterY=35.3074 CenterZ=0 NormalX=0 NormalY=0 NormalZ=1 AngleXU=0 Radius=1
    g45: Circle CenterX=61.7361 CenterY=35.9255 CenterZ=0 NormalX=0 NormalY=0 NormalZ=1 AngleXU=0 Radius=1
    g46: Circle CenterX=60.3884 CenterY=35.863 CenterZ=0 NormalX=0 NormalY=0 NormalZ=1 AngleXU=0 Radius=1
    g47: BSplineCurve PolesCount=3 KnotsCount=2 Degree=2 IsPeriodic=0
    g48: GeomPoint X=61.9939 Y=35.3074 Z=0
    g49: GeomPoint X=60.3884 Y=35.863 Z=0
    g50: Circle CenterX=61.9939 CenterY=32.3818 CenterZ=0 NormalX=0 NormalY=0 NormalZ=1 AngleXU=0 Radius=1
    g51: Circle CenterX=62.0371 CenterY=31.7538 CenterZ=0 NormalX=0 NormalY=0 NormalZ=1 AngleXU=0 Radius=1
    g52: Circle CenterX=61.3303 CenterY=31.6579 CenterZ=0 NormalX=0 NormalY=0 NormalZ=1 AngleXU=0 Radius=1
    g53: BSplineCurve PolesCount=3 KnotsCount=2 Degree=2 IsPeriodic=0
    g54: GeomPoint X=61.9939 Y=32.3818 Z=0
    g55: GeomPoint X=61.3303 Y=31.6579 Z=0
    g56: LineSegment StartX=62.0047 StartY=47.3477 StartZ=0 EndX=64.0694 EndY=47.3477 EndZ=0
    g57: LineSegment StartX=64.0694 StartY=47.3477 StartZ=0 EndX=64.0694 EndY=41.4897 EndZ=0
    g58: LineSegment StartX=61.7162 StartY=39.1365 StartZ=0 EndX=50.2517 EndY=39.1365 EndZ=0
    g59: LineSegment StartX=48.0796 StartY=41.3086 StartZ=0 EndX=48.0796 EndY=47.2867 EndZ=0
    g60: LineSegment StartX=48.0796 StartY=47.2867 StartZ=0 EndX=50.0936 EndY=47.2867 EndZ=0
    g61: LineSegment StartX=50.0936 StartY=47.2867 StartZ=0 EndX=50.0936 EndY=42.0997 EndZ=0
    g62: LineSegment StartX=50.9133 StartY=41.28 StartZ=0 EndX=55.0951 EndY=41.28 EndZ=0
    g63: LineSegment StartX=55.0951 StartY=41.28 StartZ=0 EndX=55.0951 EndY=46.912 EndZ=0
    g64: LineSegment StartX=55.0951 StartY=46.912 StartZ=0 EndX=57.0329 EndY=46.912 EndZ=0
    g65: LineSegment StartX=57.0329 StartY=46.912 StartZ=0 EndX=57.0329 EndY=41.2329 EndZ=0
    g66: LineSegment StartX=57.0329 StartY=41.2329 StartZ=0 EndX=61.2958 EndY=41.2329 EndZ=0
    g67: LineSegment StartX=62.0047 StartY=41.9418 StartZ=0 EndX=62.0047 EndY=47.3477 EndZ=0
    g68: ArcOfCircle CenterX=50.2517 CenterY=41.3086 CenterZ=0 NormalX=0 NormalY=0 NormalZ=1 AngleXU=0 Radius=2.17212 StartAngle=3.14159 EndAngle=4.71239
    g69: ArcOfCircle CenterX=50.9133 CenterY=42.0997 CenterZ=0 NormalX=0 NormalY=0 NormalZ=1 AngleXU=0 Radius=0.819674 StartAngle=3.14159 EndAngle=4.71239
    g70: ArcOfCircle CenterX=61.2958 CenterY=41.9418 CenterZ=0 NormalX=0 NormalY=0 NormalZ=1 AngleXU=0 Radius=0.708907 StartAngle=4.71239 EndAngle=6.28319
    g71: ArcOfCircle CenterX=61.7162 CenterY=41.4897 CenterZ=0 NormalX=0 NormalY=0 NormalZ=1 AngleXU=0 Radius=2.35322 StartAngle=4.71239 EndAngle=6.28319
    g72: LineSegment StartX=48.1701 StartY=48.2919 StartZ=0 EndX=48.1701 EndY=50.456 EndZ=0
    g73: LineSegment StartX=48.1701 StartY=50.456 StartZ=0 EndX=56.7961 EndY=54.1658 EndZ=0
    g74: LineSegment StartX=56.7961 StartY=54.1658 StartZ=0 EndX=47.9743 EndY=57.9962 EndZ=0
    g75: LineSegment StartX=47.9743 StartY=57.9962 StartZ=0 EndX=47.9743 EndY=59.8059 EndZ=0
    g76: LineSegment StartX=47.9743 StartY=59.8059 StartZ=0 EndX=63.9897 EndY=59.8059 EndZ=0
    g77: LineSegment StartX=63.9897 StartY=59.8059 StartZ=0 EndX=63.9897 EndY=57.6042 EndZ=0
    g78: LineSegment StartX=63.9897 StartY=57.6042 StartZ=0 EndX=54.3531 EndY=57.6042 EndZ=0
    g79: LineSegment StartX=54.3531 StartY=57.6042 StartZ=0 EndX=59.9617 EndY=55.1642 EndZ=0
    g80: LineSegment StartX=59.9617 StartY=55.1642 StartZ=0 EndX=59.9617 EndY=53.0529 EndZ=0
    g81: LineSegment StartX=59.9617 StartY=53.0529 StartZ=0 EndX=54.9165 EndY=50.7243 EndZ=0
    g82: LineSegment StartX=54.9165 StartY=50.7243 StartZ=0 EndX=64.1099 EndY=50.7243 EndZ=0
    g83: LineSegment StartX=64.1099 StartY=50.7243 StartZ=0 EndX=64.1099 EndY=48.2919 EndZ=0
    g84: LineSegment StartX=64.1099 StartY=48.2919 StartZ=0 EndX=48.1701 EndY=48.2919 EndZ=0
    g85: LineSegment StartX=61.8003 StartY=60.7665 StartZ=0 EndX=50.6821 EndY=60.7665 EndZ=0
    g86: LineSegment StartX=48.252 StartY=63.1967 StartZ=0 EndX=48.252 EndY=67.4138 EndZ=0
    g87: LineSegment StartX=50.6821 StartY=69.844 StartZ=0 EndX=61.8003 EndY=69.844 EndZ=0
    g88: LineSegment StartX=64.2304 StartY=67.4138 StartZ=0 EndX=64.2304 EndY=63.1967 EndZ=0
    g89: ArcOfCircle CenterX=50.6821 CenterY=67.4138 CenterZ=0 NormalX=0 NormalY=0 NormalZ=1 AngleXU=0 Radius=2.43016 StartAngle=1.5708 EndAngle=3.14159
    g90: ArcOfCircle CenterX=50.6821 CenterY=63.1967 CenterZ=0 NormalX=0 NormalY=0 NormalZ=1 AngleXU=0 Radius=2.43016 StartAngle=3.14159 EndAngle=4.71239
    g91: ArcOfCircle CenterX=61.8003 CenterY=63.1967 CenterZ=0 NormalX=0 NormalY=0 NormalZ=1 AngleXU=0 Radius=2.43016 StartAngle=4.71239 EndAngle=6.28319
    g92: ArcOfCircle CenterX=61.8003 CenterY=67.4138 CenterZ=0 NormalX=0 NormalY=0 NormalZ=1 AngleXU=0 Radius=2.43016 StartAngle=0 EndAngle=1.5708
    g93: LineSegment StartX=51.3443 StartY=62.91 StartZ=0 EndX=60.9044 EndY=62.91 EndZ=0
    g94: LineSegment StartX=62.0964 StartY=64.1019 StartZ=0 EndX=62.0964 EndY=66.2367 EndZ=0
    g95: LineSegment StartX=60.9044 StartY=67.4287 StartZ=0 EndX=51.3443 EndY=67.4287 EndZ=0
    g96: LineSegment StartX=50.1523 StartY=66.2367 StartZ=0 EndX=50.1523 EndY=64.1019 EndZ=0
    g97: ArcOfCircle CenterX=51.3443 CenterY=64.1019 CenterZ=0 NormalX=0 NormalY=0 NormalZ=1 AngleXU=0 Radius=1.19196 StartAngle=3.14159 EndAngle=4.71239
    g98: ArcOfCircle CenterX=51.3443 CenterY=66.2367 CenterZ=0 NormalX=0 NormalY=0 NormalZ=1 AngleXU=0 Radius=1.19196 StartAngle=1.5708 EndAngle=3.14159
    g99: ArcOfCircle CenterX=60.9044 CenterY=66.2367 CenterZ=0 NormalX=0 NormalY=0 NormalZ=1 AngleXU=0 Radius=1.19196 StartAngle=9e-16 EndAngle=1.5708
    g100: ArcOfCircle CenterX=60.9044 CenterY=64.1019 CenterZ=0 NormalX=0 NormalY=0 NormalZ=1 AngleXU=0 Radius=1.19196 StartAngle=4.71239 EndAngle=6.28319
    g101: LineSegment StartX=51.079 StartY=78.1379 StartZ=0 EndX=51.079 EndY=80.0733 EndZ=0
    g102: LineSegment StartX=51.079 StartY=80.0733 StartZ=0 EndX=50.2609 EndY=80.0733 EndZ=0
    g103: LineSegment StartX=48.4252 StartY=78.2376 StartZ=0 EndX=48.4252 EndY=73.522 EndZ=0
    g104: LineSegment StartX=50.5296 StartY=71.4176 StartZ=0 EndX=54.9302 EndY=71.4176 EndZ=0
    g105: LineSegment StartX=57.3281 StartY=73.8155 StartZ=0 EndX=57.3281 EndY=77.1032 EndZ=0
    g106: LineSegment StartX=58.3573 StartY=78.1324 StartZ=0 EndX=61.5118 EndY=78.1324 EndZ=0
    g107: LineSegment StartX=62.4299 StartY=77.2143 StartZ=0 EndX=62.4299 EndY=73.8214 EndZ=0
    g108: LineSegment StartX=61.9731 StartY=73.3647 StartZ=0 EndX=61.5027 EndY=73.3647 EndZ=0
    g109: LineSegment StartX=61.5027 StartY=73.3647 StartZ=0 EndX=61.5027 EndY=71.3589 EndZ=0
    g110: LineSegment StartX=61.5027 StartY=71.3589 StartZ=0 EndX=62.7132 EndY=71.3589 EndZ=0
    g111: LineSegment StartX=64.1972 StartY=72.8429 StartZ=0 EndX=64.1972 EndY=78.0916 EndZ=0
    g112: LineSegment StartX=62.0527 StartY=80.2361 StartZ=0 EndX=57.373 EndY=80.2361 EndZ=0
    g113: LineSegment StartX=55.3775 StartY=78.2406 StartZ=0 EndX=55.3775 EndY=74.2359 EndZ=0
    g114: LineSegment StartX=54.7254 StartY=73.5838 StartZ=0 EndX=51.2466 EndY=73.5838 EndZ=0
    g115: LineSegment StartX=50.3491 StartY=74.4813 StartZ=0 EndX=50.3491 EndY=77.713 EndZ=0
    g116: LineSegment StartX=50.774 StartY=78.1379 StartZ=0 EndX=51.079 EndY=78.1379 EndZ=0
    g117: ArcOfCircle CenterX=50.2609 CenterY=78.2376 CenterZ=0 NormalX=0 NormalY=0 NormalZ=1 AngleXU=0 Radius=1.83576 StartAngle=1.5708 EndAngle=3.14159
    g118: ArcOfCircle CenterX=50.5296 CenterY=73.522 CenterZ=0 NormalX=0 NormalY=0 NormalZ=1 AngleXU=0 Radius=2.10442 StartAngle=3.14159 EndAngle=4.71239
    g119: ArcOfCircle CenterX=50.774 CenterY=77.713 CenterZ=0 NormalX=0 NormalY=0 NormalZ=1 AngleXU=0 Radius=0.42495 StartAngle=1.5708 EndAngle=3.14159
    g120: ArcOfCircle CenterX=51.2466 CenterY=74.4813 CenterZ=0 NormalX=0 NormalY=0 NormalZ=1 AngleXU=0 Radius=0.897547 StartAngle=3.14159 EndAngle=4.71239
    g121: ArcOfCircle CenterX=54.7254 CenterY=74.2359 CenterZ=0 NormalX=0 NormalY=0 NormalZ=1 AngleXU=0 Radius=0.652069 StartAngle=4.71239 EndAngle=6.28319
    g122: ArcOfCircle CenterX=54.9302 CenterY=73.8155 CenterZ=0 NormalX=0 NormalY=0 NormalZ=1 AngleXU=0 Radius=2.39791 StartAngle=4.71239 EndAngle=6.28319
    g123: ArcOfCircle CenterX=58.3573 CenterY=77.1032 CenterZ=0 NormalX=0 NormalY=0 NormalZ=1 AngleXU=0 Radius=1.02925 StartAngle=1.5708 EndAngle=3.14159
    g124: ArcOfCircle CenterX=61.5118 CenterY=77.2143 CenterZ=0 NormalX=0 NormalY=0 NormalZ=1 AngleXU=0 Radius=0.918112 StartAngle=-9e-16 EndAngle=1.5708
    g125: ArcOfCircle CenterX=61.9731 CenterY=73.8214 CenterZ=0 NormalX=0 NormalY=0 NormalZ=1 AngleXU=0 Radius=0.456745 StartAngle=4.71239 EndAngle=6.28319
    g126: ArcOfCircle CenterX=62.7132 CenterY=72.8429 CenterZ=0 NormalX=0 NormalY=0 NormalZ=1 AngleXU=0 Radius=1.484 StartAngle=4.71239 EndAngle=6.28319
    g127: ArcOfCircle CenterX=62.0527 CenterY=78.0916 CenterZ=0 NormalX=0 NormalY=0 NormalZ=1 AngleXU=0 Radius=2.14453 StartAngle=0 EndAngle=1.5708
    g128: ArcOfCircle CenterX=57.373 CenterY=78.2406 CenterZ=0 NormalX=0 NormalY=0 NormalZ=1 AngleXU=0 Radius=1.99554 StartAngle=1.5708 EndAngle=3.14159
  constraints (207):
    c: Vertical(g0)
    c: Horizontal(g1)
    c: Horizontal(g2)
    c: Vertical(g3)
    c: Coincident(g4,g3)
    c: Horizontal(g4)
    c: Coincident(g5,g3)
    c: Vertical(g6)
    c: Vertical(g7)
    c: Coincident(g8,g7)
    c: Vertical(g9)
    c: Vertical(g10)
    c: Horizontal(g5)
    c: Coincident(g12,g4)
    c: Coincident(g12,g0)
    c: InternalAlignment(g11,g12)
    c: InternalAlignment(g13,g12)
    c: InternalAlignment(g14,g12)
    c: Weight(g15) = 1
    c: Coincident(g19,g1)
    c: Equal(g15,g16)
    c: Equal(g15,g17)
    c: Equal(g15,g18)
    c: Coincident(g19,g0)
    c: InternalAlignment(g15-g18 -> g19) x4
    c: InternalAlignment(g20,g19)
    c: InternalAlignment(g21,g19)
    c: Weight(g22) = 1
    c: Coincident(g25,g2)
    c: Equal(g22,g23)
    c: Equal(g22,g24)
    c: Coincident(g25,g10)
    c: InternalAlignment(g22,g25)
    c: InternalAlignment(g23,g25)
    c: InternalAlignment(g24,g25)
    c: InternalAlignment(g26,g25)
    c: InternalAlignment(g27,g25)
    c: Weight(g28) = 1
    c: Coincident(g31,g10)
    c: Equal(g28,g29)
    c: Equal(g28,g30)
    c: Coincident(g31,g5)
    c: InternalAlignment(g28,g31)
    c: InternalAlignment(g29,g31)
    c: InternalAlignment(g30,g31)
    c: InternalAlignment(g32,g31)
    c: InternalAlignment(g33,g31)
    c: Weight(g34) = 1
    c: Coincident(g37,g1)
    c: Equal(g34,g35)
    c: Equal(g34,g36)
    c: Coincident(g37,g9)
    c: InternalAlignment(g34,g37)
    c: InternalAlignment(g35,g37)
    c: InternalAlignment(g36,g37)
    c: InternalAlignment(g38,g37)
    c: InternalAlignment(g39,g37)
    c: Weight(g40) = 1
    c: Coincident(g41,g9)
    c: Coincident(g41,g8)
    c: InternalAlignment(g40,g41)
    c: InternalAlignment(g42,g41)
    c: InternalAlignment(g43,g41)
    c: Weight(g44) = 1
    c: Coincident(g47,g6)
    c: Equal(g44,g45)
    c: Equal(g44,g46)
    c: Coincident(g47,g7)
    c: InternalAlignment(g44,g47)
    c: InternalAlignment(g45,g47)
    c: InternalAlignment(g46,g47)
    c: InternalAlignment(g48,g47)
    c: InternalAlignment(g49,g47)
    c: Weight(g50) = 1
    c: Coincident(g53,g6)
    c: Equal(g50,g51)
    c: Equal(g50,g52)
    c: Coincident(g53,g2)
    c: InternalAlignment(g50,g53)
    c: InternalAlignment(g51,g53)
    c: InternalAlignment(g52,g53)
    c: InternalAlignment(g54,g53)
    c: InternalAlignment(g55,g53)
    c: Horizontal(g56)
    c: Coincident(g56,g57)
    c: Vertical(g57)
    c: Horizontal(g58)
    c: Vertical(g59)
    c: Coincident(g59,g60)
    c: Coincident(g60,g61)
    c: Vertical(g61)
    c: Horizontal(g62)
    c: Coincident(g62,g63)
    c: Vertical(g63)
    c: Coincident(g63,g64)
    c: Horizontal(g64)
    c: Coincident(g64,g65)
    c: Coincident(g65,g66)
    c: Horizontal(g66)
    c: Coincident(g67,g56)
    c: Horizontal(g60)
    c: Vertical(g65)
    c: Vertical(g67)
    c: Tangent(g59,g68) = 1.5708
    c: Tangent(g58,g68) = 1.5708
    c: Tangent(g61,g69) = -1.5708
    c: Tangent(g62,g69) = -1.5708
    c: Tangent(g66,g70) = -1.5708
    c: Tangent(g67,g70) = -1.5708
    c: Tangent(g57,g71) = 1.5708
    c: Tangent(g58,g71) = 1.5708
    c: Vertical(g72)
    c: Coincident(g72,g73)
    c: Coincident(g73,g74)
    c: Coincident(g74,g75)
    c: Vertical(g75)
    c: Coincident(g75,g76)
    c: Horizontal(g76)
    c: Coincident(g76,g77)
    c: Vertical(g77)
    c: Coincident(g77,g78)
    c: Horizontal(g78)
    c: Coincident(g78,g79)
    c: Coincident(g79,g80)
    c: Vertical(g80)
    c: Coincident(g80,g81)
    c: Coincident(g81,g82)
    c: Horizontal(g82)
    c: Coincident(g82,g83)
    c: Vertical(g83)
    c: Coincident(g83,g84)
    c: Coincident(g84,g72)
    c: Horizontal(g84)
    c: Horizontal(g85)
    c: Horizontal(g87)
    c: Vertical(g86)
    c: Vertical(g88)
    c: Tangent(g86,g89) = 1.5708
    c: Tangent(g87,g89) = 1.5708
    c: Tangent(g86,g90) = 1.5708
    c: Tangent(g85,g90) = 1.5708
    c: Tangent(g85,g91) = 1.5708
    c: Tangent(g88,g91) = 1.5708
    c: Tangent(g88,g92) = 1.5708
    c: Tangent(g87,g92) = 1.5708
    c: Equal(g90,g89)
    c: Equal(g89,g92)
    c: Equal(g92,g91)
    c: Horizontal(g93)
    c: Horizontal(g95)
    c: Vertical(g94)
    c: Vertical(g96)
    c: Tangent(g96,g97) = -1.5708
    c: Tangent(g93,g97) = -1.5708
    c: Tangent(g96,g98) = -1.5708
    c: Tangent(g95,g98) = -1.5708
    c: Tangent(g95,g99) = -1.5708
    c: Tangent(g94,g99) = -1.5708
    c: Tangent(g94,g100) = -1.5708
    c: Tangent(g93,g100) = -1.5708
    c: Equal(g100,g99)
    c: Equal(g99,g98)
    c: Equal(g98,g97)
    c: Vertical(g101)
    c: Coincident(g101,g102)
    c: Horizontal(g102)
    c: Vertical(g103)
    c: Horizontal(g104)
    c: Vertical(g105)
    c: Vertical(g107)
    c: Coincident(g108,g109)
    c: Vertical(g109)
    c: Coincident(g109,g110)
    c: Horizontal(g110)
    c: Vertical(g111)
    c: Vertical(g113)
    c: Horizontal(g114)
    c: Vertical(g115)
    c: Coincident(g116,g101)
    c: Tangent(g102,g117) = -1.5708
    c: Tangent(g103,g117) = -1.5708
    c: Horizontal(g116)
    c: Tangent(g103,g118) = -1.5708
    c: Tangent(g104,g118) = -1.5708
    c: Tangent(g116,g119) = 1.5708
    c: Tangent(g115,g119) = 1.5708
    c: Tangent(g115,g120) = 1.5708
    c: Tangent(g114,g120) = 1.5708
    c: Tangent(g113,g121) = 1.5708
    c: Tangent(g114,g121) = 1.5708
    c: Tangent(g105,g122) = -1.5708
    c: Tangent(g104,g122) = -1.5708
    c: Tangent(g105,g123) = 1.5708
    c: Tangent(g106,g123) = 1.5708
    c: Horizontal(g106)
    c: Tangent(g107,g124) = 1.5708
    c: Tangent(g106,g124) = 1.5708
    c: Horizontal(g108)
    c: Tangent(g107,g125) = 1.5708
    c: Tangent(g108,g125) = 1.5708
    c: Tangent(g110,g126) = -1.5708
    c: Tangent(g111,g126) = -1.5708
    c: Horizontal(g112)
    c: Tangent(g111,g127) = -1.5708
    c: Tangent(g112,g127) = -1.5708
    c: Tangent(g112,g128) = -1.5708
    c: Tangent(g113,g128) = -1.5708
FEATURE [PartDesign::Pocket] Pocket011
  BaseFeature = -> Pocket010
  Direction = (1,0,0)
  Length = 2
  Length2 = 5
  Profile = -> Sketch034
  ReferenceAxis = -> Sketch034 [N_Axis]
  Type = 0
FEATURE [Part::Compound] Compound  label="powerbank"
  Links = -> [Part__Feature,Part002,Part__Feature006,_SS1022_Z]
  Placement = pos=(-121,17,26) rot=(0,1,0;3.14159rad)
FEATURE [Sketcher::SketchObject] Sketch035
  ExternalGeometry = -> [Pocket007]
  FullyConstrained = true
  MapMode = 5
  Placement = pos=(0,0,5) rot=(0,0,1;0rad)
  Support = -> [Pocket007]
  sketch-geometry (12):
    g0: Circle CenterX=121.052 CenterY=60.9871 CenterZ=0 NormalX=0 NormalY=0 NormalZ=1 AngleXU=0 Radius=1.5
    g1: LineSegment StartX=121.052 StartY=60.9871 StartZ=0 EndX=121.052 EndY=68.9871 EndZ=0
    g2: LineSegment StartX=121.052 StartY=60.9871 StartZ=0 EndX=129.052 EndY=60.9871 EndZ=0
    g3: Circle CenterX=-121.02 CenterY=60.9871 CenterZ=0 NormalX=0 NormalY=0 NormalZ=1 AngleXU=0 Radius=1.5
    g4: LineSegment StartX=-121.02 StartY=60.9871 StartZ=0 EndX=-121.02 EndY=68.9871 EndZ=0
    g5: LineSegment StartX=-121.02 StartY=60.9871 StartZ=0 EndX=-129.02 EndY=60.9871 EndZ=0
    g6: Circle CenterX=-121.02 CenterY=-61.0468 CenterZ=0 NormalX=0 NormalY=0 NormalZ=1 AngleXU=0 Radius=1.5
    g7: LineSegment StartX=-121.02 StartY=-61.0468 StartZ=0 EndX=-121.02 EndY=-69.0468 EndZ=0
    g8: LineSegment StartX=-121.02 StartY=-61.0468 StartZ=0 EndX=-129.02 EndY=-61.0468 EndZ=0
    g9: Circle CenterX=121.052 CenterY=-61.0468 CenterZ=0 NormalX=0 NormalY=0 NormalZ=1 AngleXU=0 Radius=1.5
    g10: LineSegment StartX=121.052 StartY=-61.0468 StartZ=0 EndX=129.052 EndY=-61.0468 EndZ=0
    g11: LineSegment StartX=121.052 StartY=-61.0468 StartZ=0 EndX=121.052 EndY=-69.0468 EndZ=0
  constraints (36):
    c: Radius(g0) = 1.5
    c: Coincident(g1,g0)
    c: PointOnObject(g1,g-4)
    c: Vertical(g1)
    c: Coincident(g2,g0)
    c: PointOnObject(g2,g-3)
    c: Horizontal(g2)
    c: DistanceY(g1,g1) = 8
    c: DistanceX(g2,g2) = 8
    c: Coincident(g4,g3)
    c: PointOnObject(g4,g-4)
    c: Vertical(g4)
    c: Coincident(g5,g3)
    c: PointOnObject(g5,g-5)
    c: Horizontal(g5)
    c: Radius(g3) = 1.5
    c: DistanceY(g4,g4) = 8
    c: DistanceX(g5,g5) = 8
    c: Coincident(g7,g6)
    c: PointOnObject(g7,g-6)
    c: Vertical(g7)
    c: Coincident(g8,g6)
    c: PointOnObject(g8,g-5)
    c: Horizontal(g8)
    c: Radius(g6) = 1.5
    c: DistanceX(g8,g8) = 8
    c: DistanceY(g7,g7) = 8
    c: Radius(g9) = 1.5
    c: Coincident(g10,g9)
    c: PointOnObject(g10,g-3)
    c: Horizontal(g10)
    c: Coincident(g11,g9)
    c: PointOnObject(g11,g-6)
    c: Vertical(g11)
    c: DistanceX(g10,g10) = 8
    c: DistanceY(g11,g11) = 8
FEATURE [PartDesign::Hole] Hole
  BaseFeature = -> Pocket007
  CustomThreadClearance = 0
  Depth = 25
  DepthType = 0
  Diameter = 3.4
  DrillForDepth = false
  DrillPoint = 1
  DrillPointAngle = 118
  HoleCutCountersinkAngle = 90
  HoleCutCustomValues = false
  HoleCutDepth = 2.1
  HoleCutDiameter = 6.1
  HoleCutType = 1
  ModelThread = false
  Profile = -> Sketch035
  Tapered = false
  TaperedAngle = 90
  ThreadClass = 0
  ThreadDepth = 25
  ThreadDepthType = 0
  ThreadDirection = 0
  ThreadFit = 0
  ThreadSize = 9
  ThreadType = 1
  Threaded = false
  UseCustomThreadClearance = false
FEATURE [PartDesign::Body] Body003  label="TAPA CAJA"
  Group = -> [Sketch017,Pad012,Sketch028,Pocket005,Sketch030,Pocket007,Sketch035,Hole]
  Origin = -> Origin007
  Placement = pos=(0,0,110) rot=(0,0,1;0rad)
  Tip = -> Hole
FEATURE [Part::Feature] Part__Feature007  label="Cam V2.1 v1"
  Placement = pos=(48.9647,2e-15,44.8637) rot=(0.983106,-0.129428,0.129428;1.58783rad)
  shape: bbox 10.53 x 25 x 23.44 mm, 247 faces (baked)
FEATURE [Sketcher::SketchObject] Sketch036
  FullyConstrained = true
  MapMode = 5
  Placement = pos=(0,0,0) rot=(0.57735,0.57735,0.57735;2.0944rad)
  Support = -> [YZ_Plane010]
  sketch-geometry (9):
    g0: LineSegment StartX=-23 StartY=50 StartZ=0 EndX=-21 EndY=50 EndZ=0
    g1: LineSegment StartX=-21 StartY=50 StartZ=0 EndX=-21 EndY=2 EndZ=0
    g2: LineSegment StartX=-21 StartY=2 StartZ=0 EndX=21 EndY=2 EndZ=0
    g3: LineSegment StartX=21 StartY=2 StartZ=0 EndX=21 EndY=50 EndZ=0
    g4: LineSegment StartX=21 StartY=50 StartZ=0 EndX=23 EndY=50 EndZ=0
    g5: LineSegment StartX=23 StartY=50 StartZ=0 EndX=23 EndY=0 EndZ=0
    g6: LineSegment StartX=23 StartY=0 StartZ=0 EndX=-23 EndY=0 EndZ=0
    g7: LineSegment StartX=-23 StartY=0 StartZ=0 EndX=-23 EndY=50 EndZ=0
    g8: LineSegment StartX=-21 StartY=2 StartZ=0 EndX=-21 EndY=0 EndZ=0
  constraints (26):
    c: Horizontal(g0)
    c: Coincident(g0,g1)
    c: Coincident(g1,g2)
    c: Horizontal(g2)
    c: Coincident(g2,g3)
    c: Coincident(g3,g4)
    c: Horizontal(g4)
    c: Coincident(g4,g5)
    c: Vertical(g5)
    c: Coincident(g5,g6)
    c: Horizontal(g6)
    c: Coincident(g6,g7)
    c: Coincident(g7,g0)
    c: Vertical(g7)
    c: Vertical(g1)
    c: Vertical(g3)
    c: Equal(g0,g4)
    c: Symmetric(g6,g5,g-1)
    c: Equal(g7,g5)
    c: Coincident(g8,g1)
    c: PointOnObject(g8,g6)
    c: Vertical(g8)
    c: DistanceX(g0,g0) = 2
    c: DistanceX(g6,g6) = 46
    c: DistanceY(g8,g8) = 2
    c: DistanceY(g5,g5) = 50
FEATURE [PartDesign::Pad] Pad020
  Direction = (1,1,1)
  Length = 30
  Length2 = 100
  Placement = pos=(0,0,0) rot=(0.57735,0.57735,0.57735;2.0944rad)
  Profile = -> Sketch036
  Refine = true
  Type = 0
FEATURE [Sketcher::SketchObject] Sketch004
  ExternalGeometry = -> [Pad020]
  FullyConstrained = true
  MapMode = 5
  Placement = pos=(-1.01e-14,-23,5.1e-15) rot=(-0.57735,-0.57735,0.57735;4.18879rad)
  Support = -> [Pad020]
  sketch-geometry (3):
    g0: Circle CenterX=-35 CenterY=15 CenterZ=0 NormalX=0 NormalY=0 NormalZ=1 AngleXU=0 Radius=1.25
    g1: LineSegment StartX=-35 StartY=15 StartZ=0 EndX=-35 EndY=-8.9e-15 EndZ=0
    g2: LineSegment StartX=-35 StartY=15 StartZ=0 EndX=-7.1e-15 EndY=15 EndZ=0
  constraints (9):
    c: Radius(g0) = 1.25
    c: Coincident(g1,g0)
    c: PointOnObject(g1,g-4)
    c: Vertical(g1)
    c: Coincident(g2,g0)
    c: PointOnObject(g2,g-5)
    c: Horizontal(g2)
    c: DistanceX(g2,g2) = 35
    c: DistanceY(g1,g1) = 15
FEATURE [PartDesign::Hole] Hole003
  BaseFeature = -> Pad020
  CustomThreadClearance = 0
  Depth = 25
  DepthType = 1
  Diameter = 6
  DrillForDepth = false
  DrillPoint = 1
  DrillPointAngle = 118
  HoleCutCountersinkAngle = 90
  HoleCutCustomValues = false
  HoleCutDepth = 0
  HoleCutDiameter = 6.1
  HoleCutType = 0
  ModelThread = false
  Placement = pos=(0,0,0) rot=(0.57735,0.57735,0.57735;2.0944rad)
  Profile = -> Sketch004
  Refine = true
  Tapered = false
  TaperedAngle = 90
  ThreadClass = 0
  ThreadDepth = 23.5
  ThreadDepthType = 0
  ThreadDirection = 0
  ThreadFit = 0
  ThreadSize = 0
  ThreadType = 0
  Threaded = false
  UseCustomThreadClearance = false
FEATURE [PartDesign::Fillet] Fillet
  Base = -> Hole003 [Edge20,Edge4,Edge3,Edge15]
  BaseFeature = -> Hole003
  Placement = pos=(0,0,0) rot=(0.57735,0.57735,0.57735;2.0944rad)
  Radius = 14
  Refine = true
  SupportTransform = false
  UseAllEdges = false
FEATURE [PartDesign::Fillet] Fillet011
  Base = -> Fillet [Edge31,Edge17]
  BaseFeature = -> Fillet
  Placement = pos=(0,0,0) rot=(0.57735,0.57735,0.57735;2.0944rad)
  Radius = 3
  Refine = true
  SupportTransform = false
  UseAllEdges = false
FEATURE [PartDesign::Fillet] Fillet012
  Base = -> Fillet011 [Edge35,Edge37]
  BaseFeature = -> Fillet011
  Placement = pos=(0,0,0) rot=(0.57735,0.57735,0.57735;2.0944rad)
  Radius = 2
  Refine = true
  SupportTransform = false
  UseAllEdges = false
FEATURE [Sketcher::SketchObject] Sketch003
  FullyConstrained = false
  MapMode = 5
  Placement = pos=(-1.1e-14,-25,8e-15) rot=(0.57735,0.57735,-0.57735;2.0944rad)
  sketch-geometry (3):
    g0: Circle CenterX=-35 CenterY=15 CenterZ=0 NormalX=0 NormalY=0 NormalZ=1 AngleXU=0 Radius=1.25
    g1: LineSegment StartX=-35 StartY=15 StartZ=0 EndX=-7.1e-15 EndY=15 EndZ=0
    g2: LineSegment StartX=-35 StartY=15 StartZ=0 EndX=-35 EndY=30 EndZ=0
  constraints (7):
    c: Radius(g0) = 1.25
    c: Coincident(g1,g0)
    c: Horizontal(g1)
    c: Coincident(g2,g0)
    c: Vertical(g2)
    c: DistanceX(g1,g1) = 35
    c: DistanceY(g2,g2) = 15
FEATURE [Sketcher::SketchObject] Sketch002
  FullyConstrained = true
  MapMode = 5
  Placement = pos=(0,0,0) rot=(0.57735,0.57735,0.57735;2.0944rad)
  Support = -> [YZ_Plane011]
  sketch-geometry (9):
    g0: LineSegment StartX=-25 StartY=50 StartZ=0 EndX=-23 EndY=50 EndZ=0
    g1: LineSegment StartX=-23 StartY=50 StartZ=0 EndX=-23 EndY=2 EndZ=0
    g2: LineSegment StartX=-23 StartY=2 StartZ=0 EndX=23 EndY=2 EndZ=0
    g3: LineSegment StartX=23 StartY=2 StartZ=0 EndX=23 EndY=50 EndZ=0
    g4: LineSegment StartX=23 StartY=50 StartZ=0 EndX=25 EndY=50 EndZ=0
    g5: LineSegment StartX=25 StartY=50 StartZ=0 EndX=25 EndY=0 EndZ=0
    g6: LineSegment StartX=25 StartY=0 StartZ=0 EndX=-25 EndY=0 EndZ=0
    g7: LineSegment StartX=-25 StartY=0 StartZ=0 EndX=-25 EndY=50 EndZ=0
    g8: LineSegment StartX=-23 StartY=2 StartZ=0 EndX=-23 EndY=0 EndZ=0
  constraints (26):
    c: Horizontal(g0)
    c: Coincident(g0,g1)
    c: Coincident(g1,g2)
    c: Horizontal(g2)
    c: Coincident(g2,g3)
    c: Coincident(g3,g4)
    c: Horizontal(g4)
    c: Coincident(g4,g5)
    c: Vertical(g5)
    c: Coincident(g5,g6)
    c: Horizontal(g6)
    c: Coincident(g6,g7)
    c: Coincident(g7,g0)
    c: Vertical(g7)
    c: Vertical(g1)
    c: Vertical(g3)
    c: Equal(g0,g4)
    c: Symmetric(g6,g5,g-1)
    c: Equal(g7,g5)
    c: Coincident(g8,g1)
    c: PointOnObject(g8,g6)
    c: Vertical(g8)
    c: DistanceX(g0,g0) = 2
    c: DistanceX(g6,g6) = 50
    c: DistanceY(g8,g8) = 2
    c: DistanceY(g5,g5) = 50
FEATURE [PartDesign::Pad] Pad021
  Direction = (1,1,1)
  Length = 30
  Length2 = 100
  Placement = pos=(0,0,0) rot=(0.57735,0.57735,0.57735;2.0944rad)
  Profile = -> Sketch002
  Refine = true
  Type = 0
FEATURE [PartDesign::Hole] Hole004
  BaseFeature = -> Pad021
  CustomThreadClearance = 0
  Depth = 25
  DepthType = 1
  Diameter = 6
  DrillForDepth = false
  DrillPoint = 1
  DrillPointAngle = 118
  HoleCutCountersinkAngle = 90
  HoleCutCustomValues = false
  HoleCutDepth = 0
  HoleCutDiameter = 6.1
  HoleCutType = 0
  ModelThread = false
  Placement = pos=(0,0,0) rot=(0.57735,0.57735,0.57735;2.0944rad)
  Profile = -> Sketch003
  Refine = true
  Tapered = false
  TaperedAngle = 90
  ThreadClass = 0
  ThreadDepth = 23.5
  ThreadDepthType = 0
  ThreadDirection = 0
  ThreadFit = 0
  ThreadSize = 0
  ThreadType = 0
  Threaded = false
  UseCustomThreadClearance = false
FEATURE [PartDesign::Fillet] Fillet008
  Base = -> Hole004 [Edge20,Edge4,Edge3,Edge15]
  BaseFeature = -> Hole004
  Placement = pos=(0,0,0) rot=(0.57735,0.57735,0.57735;2.0944rad)
  Radius = 14
  Refine = true
  SupportTransform = false
  UseAllEdges = false
FEATURE [PartDesign::Fillet] Fillet009
  Base = -> Fillet008 [Edge17,Edge31]
  BaseFeature = -> Fillet008
  Placement = pos=(0,0,0) rot=(0.57735,0.57735,0.57735;2.0944rad)
  Radius = 3
  Refine = true
  SupportTransform = false
  UseAllEdges = false
FEATURE [PartDesign::Fillet] Fillet010
  Base = -> Fillet009 [Edge37,Edge35]
  BaseFeature = -> Fillet009
  Placement = pos=(0,0,0) rot=(0.57735,0.57735,0.57735;2.0944rad)
  Radius = 2
  Refine = true
  SupportTransform = false
  UseAllEdges = false
FEATURE [Sketcher::SketchObject] Sketch005
  FullyConstrained = true
  MapMode = 5
  Placement = pos=(0,0,-1e-16) rot=(0.707107,0.707107,0;3.14159rad)
  Support = -> [Fillet010]
FEATURE [PartDesign::Body] Body005
  Group = -> [Sketch036,Pad020,Sketch004,Hole003,Fillet,Fillet011,Fillet012,Sketch005]
  Origin = -> Origin010
  Tip = -> Fillet012
FEATURE [App::Part] Part003
  Group = -> [Body005]
  Origin = -> Origin009
FEATURE [PartDesign::Body] Body006
  Group = -> [Sketch002,Pad021,Sketch003,Hole004,Fillet008,Fillet009,Fillet010]
  Origin = -> Origin012
  Tip = -> Fillet010
FEATURE [App::Part] Part004
  Group = -> [Body006]
  Origin = -> Origin011
  Placement = pos=(52.5003,0,29.9874) rot=(0,-1,0;1.8326rad)
FEATURE [Sketcher::SketchObject] Sketch037
  FullyConstrained = true
  MapMode = 5
  Support = -> [XY_Plane013]
  sketch-geometry (4):
    g0: LineSegment StartX=-55 StartY=55 StartZ=0 EndX=55 EndY=55 EndZ=0
    g1: LineSegment StartX=55 StartY=55 StartZ=0 EndX=55 EndY=-55 EndZ=0
    g2: LineSegment StartX=55 StartY=-55 StartZ=0 EndX=-55 EndY=-55 EndZ=0
    g3: LineSegment StartX=-55 StartY=-55 StartZ=0 EndX=-55 EndY=55 EndZ=0
  constraints (10):
    c: Coincident(g0,g1)
    c: Coincident(g1,g2)
    c: Coincident(g2,g3)
    c: Coincident(g3,g0)
    c: Horizontal(g2)
    c: Vertical(g1)
    c: DistanceX(g0,g0) = 110
    c: DistanceY(g1,g1) = 110
    c: Symmetric(g0,g0,g-2)
    c: Symmetric(g2,g0,g-1)
FEATURE [PartDesign::Pad] Pad002
  Direction = (0,0,1)
  Length = 220
  Length2 = 10
  Profile = -> Sketch037
  ReferenceAxis = -> Sketch037 [N_Axis]
  Type = 0
FEATURE [Sketcher::SketchObject] Sketch038
  FullyConstrained = true
  MapMode = 5
  Placement = pos=(0,-55,0) rot=(1,0,0;1.5708rad)
  Support = -> [Pad002]
  sketch-geometry (18):
    g0: GeomPoint X=0 Y=220 Z=0
    g1: GeomPoint X=-25.5 Y=220 Z=0
    g2: GeomPoint X=25.5 Y=220 Z=0
    g3: GeomPoint X=0 Y=20 Z=0
    g4: GeomPoint X=-55 Y=20 Z=0
    g5: GeomPoint X=55 Y=20 Z=0
    g6: GeomPoint X=-25.5 Y=200 Z=0
    g7: GeomPoint X=25.5 Y=200 Z=0
    g8: GeomPoint X=-55 Y=220 Z=0
    g9: GeomPoint X=55 Y=220 Z=0
    g10: LineSegment StartX=-55 StartY=20 StartZ=0 EndX=-25.5 EndY=200 EndZ=0
    g11: LineSegment StartX=-25.5 StartY=220 StartZ=0 EndX=-25.5 EndY=200 EndZ=0
    g12: LineSegment StartX=-55 StartY=220 StartZ=0 EndX=-25.5 EndY=220 EndZ=0
    g13: LineSegment StartX=-55 StartY=220 StartZ=0 EndX=-55 EndY=20 EndZ=0
    g14: LineSegment StartX=25.5 StartY=220 StartZ=0 EndX=55 EndY=220 EndZ=0
    g15: LineSegment StartX=55 StartY=20 StartZ=0 EndX=55 EndY=220 EndZ=0
    g16: LineSegment StartX=55 StartY=20 StartZ=0 EndX=25.5 EndY=200 EndZ=0
    g17: LineSegment StartX=25.5 StartY=200 StartZ=0 EndX=25.5 EndY=220 EndZ=0
  constraints (34):
    c: Vertical(g-1,g0)
    c: DistanceY(g-1,g0) = 220
    c: Horizontal(g2,g0)
    c: DistanceX(g1,g2) = 51
    c: Symmetric(g1,g2,g-2)
    c: Vertical(g-1,g3)
    c: DistanceY(g-1,g3) = 20
    c: Horizontal(g3,g5)
    c: DistanceX(g4,g5) = 110
    c: Symmetric(g4,g5,g-2)
    c: Vertical(g7,g2)
    c: Vertical(g6,g1)
    c: Horizontal(g7,g6)
    c: DistanceY(g7,g2) = 20
    c: Vertical(g9,g5)
    c: Vertical(g4,g8)
    c: Horizontal(g8,g0)
    c: Horizontal(g9,g2)
    c: Coincident(g10,g4)
    c: Coincident(g10,g6)
    c: Coincident(g11,g1)
    c: Coincident(g11,g10)
    c: Coincident(g12,g8)
    c: Coincident(g12,g11)
    c: Coincident(g13,g12)
    c: Coincident(g13,g10)
    c: Coincident(g14,g2)
    c: Coincident(g14,g9)
    c: Coincident(g15,g5)
    c: Coincident(g15,g14)
    c: Coincident(g16,g15)
    c: Coincident(g16,g7)
    c: Coincident(g17,g16)
    c: Coincident(g17,g14)
FEATURE [PartDesign::Pocket] Pocket012
  BaseFeature = -> Pad002
  Direction = (0,1,-2e-16)
  Length = 158
  Length2 = 5
  Profile = -> Sketch038
  ReferenceAxis = -> Sketch038 [N_Axis]
  Type = 0
FEATURE [PartDesign::Plane] DatumPlane
  Length = 152.006
  MapMode = 5
  Placement = pos=(55,0,0) rot=(0.57735,0.57735,0.57735;2.0944rad)
  ResizeMode = 0
  Support = -> [Pocket012]
  Width = 279.006
FEATURE [Sketcher::SketchObject] Sketch008
  FullyConstrained = true
  MapMode = 5
  Placement = pos=(55,0,0) rot=(0.57735,0.57735,0.57735;2.0944rad)
  Support = -> [DatumPlane]
  sketch-geometry (18):
    g0: GeomPoint X=0 Y=220 Z=0
    g1: GeomPoint X=-15.5 Y=220 Z=0
    g2: GeomPoint X=15.5 Y=220 Z=0
    g3: GeomPoint X=-15.5 Y=200 Z=0
    g4: GeomPoint X=15.5 Y=200 Z=0
    g5: GeomPoint X=0 Y=20 Z=0
    g6: GeomPoint X=-55 Y=20 Z=0
    g7: GeomPoint X=55 Y=20 Z=0
    g8: GeomPoint X=-55 Y=220 Z=0
    g9: GeomPoint X=55 Y=220 Z=0
    g10: LineSegment StartX=-55 StartY=20 StartZ=0 EndX=-15.5 EndY=200 EndZ=0
    g11: LineSegment StartX=-15.5 StartY=220 StartZ=0 EndX=-15.5 EndY=200 EndZ=0
    g12: LineSegment StartX=-55 StartY=220 StartZ=0 EndX=-15.5 EndY=220 EndZ=0
    g13: LineSegment StartX=-55 StartY=220 StartZ=0 EndX=-55 EndY=20 EndZ=0
    g14: LineSegment StartX=15.5 StartY=220 StartZ=0 EndX=15.5 EndY=200 EndZ=0
    g15: LineSegment StartX=15.5 StartY=200 StartZ=0 EndX=55 EndY=20 EndZ=0
    g16: LineSegment StartX=55 StartY=20 StartZ=0 EndX=55 EndY=220 EndZ=0
    g17: LineSegment StartX=55 StartY=220 StartZ=0 EndX=15.5 EndY=220 EndZ=0
  constraints (34):
    c: Vertical(g0,g-1)
    c: DistanceY(g-1,g0) = 220
    c: Horizontal(g2,g0)
    c: DistanceX(g1,g2) = 31
    c: Symmetric(g1,g2,g-2)
    c: Vertical(g3,g1)
    c: Vertical(g4,g2)
    c: Horizontal(g4,g3)
    c: DistanceY(g4,g2) = 20
    c: Vertical(g-1,g5)
    c: DistanceY(g-1,g5) = 20
    c: Horizontal(g7,g5)
    c: DistanceX(g6,g7) = 110
    c: Symmetric(g6,g7,g-2)
    c: Horizontal(g9,g2)
    c: Horizontal(g8,g1)
    c: Vertical(g9,g7)
    c: Vertical(g6,g8)
    c: Coincident(g10,g6)
    c: Coincident(g10,g3)
    c: Coincident(g11,g1)
    c: Coincident(g11,g10)
    c: Coincident(g12,g8)
    c: Coincident(g12,g11)
    c: Coincident(g13,g12)
    c: Coincident(g13,g10)
    c: Coincident(g14,g2)
    c: Coincident(g14,g4)
    c: Coincident(g15,g14)
    c: Coincident(g15,g7)
    c: Coincident(g16,g15)
    c: Coincident(g16,g9)
    c: Coincident(g17,g16)
    c: Coincident(g17,g14)
FEATURE [PartDesign::Pocket] Pocket001
  BaseFeature = -> Pocket012
  Direction = (-1,0,0)
  Length = 158
  Length2 = 5
  Profile = -> Sketch008
  ReferenceAxis = -> Sketch008 [N_Axis]
  Type = 0
FEATURE [PartDesign::Thickness] Thickness001
  Base = -> Pocket001 [Face13]
  BaseFeature = -> Pocket001
  Intersection = false
  Join = 0
  Mode = 0
  SupportTransform = false
  Value = 4
FEATURE [Sketcher::SketchObject] Sketch014
  FullyConstrained = true
  MapMode = 5
  Placement = pos=(0,59,0) rot=(0,0.707107,0.707107;3.14159rad)
  Support = -> [Thickness001]
  sketch-geometry (4):
    g0: LineSegment StartX=-55 StartY=4 StartZ=0 EndX=55 EndY=4 EndZ=0
    g1: LineSegment StartX=55 StartY=4 StartZ=0 EndX=55 EndY=0 EndZ=0
    g2: LineSegment StartX=55 StartY=0 StartZ=0 EndX=-55 EndY=0 EndZ=0
    g3: LineSegment StartX=-55 StartY=0 StartZ=0 EndX=-55 EndY=4 EndZ=0
  constraints (11):
    c: Coincident(g0,g1)
    c: Coincident(g1,g2)
    c: Coincident(g2,g3)
    c: Coincident(g3,g0)
    c: Horizontal(g0)
    c: Vertical(g1)
    c: Vertical(g3)
    c: DistanceX(g2,g2) = 110
    c: Symmetric(g1,g2,g-2)
    c: Horizontal(g1,g-1)
    c: DistanceY(g1,g1) = 4
FEATURE [PartDesign::Pocket] Pocket013
  BaseFeature = -> Thickness001
  Direction = (0,-1,2e-16)
  Length = 4
  Length2 = 5
  Profile = -> Sketch014
  ReferenceAxis = -> Sketch014 [N_Axis]
  Type = 0
FEATURE [Sketcher::SketchObject] Sketch016
  FullyConstrained = true
  MapMode = 5
  Placement = pos=(0,-55,0) rot=(0,0.707107,0.707107;3.14159rad)
  Support = -> [Pocket013]
  sketch-geometry (8):
    g0: LineSegment StartX=-55 StartY=7 StartZ=0 EndX=-52 EndY=7 EndZ=0
    g1: LineSegment StartX=-52 StartY=7 StartZ=0 EndX=-52 EndY=4 EndZ=0
    g2: LineSegment StartX=-52 StartY=4 StartZ=0 EndX=-55 EndY=4 EndZ=0
    g3: LineSegment StartX=-55 StartY=4 StartZ=0 EndX=-55 EndY=7 EndZ=0
    g4: LineSegment StartX=52 StartY=7 StartZ=0 EndX=55 EndY=7 EndZ=0
    g5: LineSegment StartX=55 StartY=7 StartZ=0 EndX=55 EndY=4 EndZ=0
    g6: LineSegment StartX=55 StartY=4 StartZ=0 EndX=52 EndY=4 EndZ=0
    g7: LineSegment StartX=52 StartY=4 StartZ=0 EndX=52 EndY=7 EndZ=0
  constraints (23):
    c: Coincident(g0,g1)
    c: Coincident(g1,g2)
    c: Coincident(g2,g3)
    c: Coincident(g3,g0)
    c: Horizontal(g0)
    c: Horizontal(g2)
    c: Vertical(g1)
    c: Vertical(g3)
    c: Coincident(g4,g5)
    c: Coincident(g5,g6)
    c: Coincident(g6,g7)
    c: Coincident(g7,g4)
    c: Horizontal(g4)
    c: Horizontal(g6)
    c: Vertical(g5)
    c: Vertical(g7)
    c: DistanceY(g1,g1) = 3
    c: DistanceY(g7,g7) = 3
    c: DistanceX(g4,g4) = 3
    c: DistanceX(g0,g0) = 3
    c: DistanceX(g2,g5) = 110
    c: Symmetric(g2,g5,g-2)
    c: DistanceY(g-1,g6) = 4
FEATURE [PartDesign::Pad] Pad022
  BaseFeature = -> Pocket013
  Direction = (0,1,-2e-16)
  Length = 110
  Length2 = 10
  Profile = -> Sketch016
  ReferenceAxis = -> Sketch016 [N_Axis]
  Type = 0
FEATURE [Sketcher::SketchObject] Sketch018
  FullyConstrained = true
  MapMode = 5
  Placement = pos=(0,59,0) rot=(0,0.707107,0.707107;3.14159rad)
  Support = -> [Pad022]
  sketch-geometry (4):
    g0: LineSegment StartX=-55 StartY=20 StartZ=0 EndX=55 EndY=20 EndZ=0
    g1: LineSegment StartX=55 StartY=20 StartZ=0 EndX=55 EndY=4 EndZ=0
    g2: LineSegment StartX=55 StartY=4 StartZ=0 EndX=-55 EndY=4 EndZ=0
    g3: LineSegment StartX=-55 StartY=4 StartZ=0 EndX=-55 EndY=20 EndZ=0
  constraints (11):
    c: Coincident(g0,g1)
    c: Coincident(g1,g2)
    c: Coincident(g2,g3)
    c: Coincident(g3,g0)
    c: Horizontal(g2)
    c: Vertical(g1)
    c: Vertical(g3)
    c: Symmetric(g0,g0,g-2)
    c: DistanceX(g0,g0) = 110
    c: DistanceY(g1,g1) = 16
    c: DistanceY(g-1,g1) = 4
FEATURE [PartDesign::Pocket] Pocket014
  BaseFeature = -> Pad022
  Direction = (0,-1,2e-16)
  Length = 4
  Length2 = 5
  Profile = -> Sketch018
  ReferenceAxis = -> Sketch018 [N_Axis]
  Type = 0
FEATURE [Sketcher::SketchObject] Sketch019
  FullyConstrained = true
  MapMode = 5
  Placement = pos=(55,0,0) rot=(0.57735,-0.57735,-0.57735;2.0944rad)
  Support = -> [Pocket014]
  sketch-geometry (4):
    g0: LineSegment StartX=-55 StartY=20 StartZ=0 EndX=-52 EndY=20 EndZ=0
    g1: LineSegment StartX=-52 StartY=20 StartZ=0 EndX=-52 EndY=15 EndZ=0
    g2: LineSegment StartX=-52 StartY=15 StartZ=0 EndX=-55 EndY=15 EndZ=0
    g3: LineSegment StartX=-55 StartY=15 StartZ=0 EndX=-55 EndY=20 EndZ=0
  constraints (12):
    c: Coincident(g0,g1)
    c: Coincident(g1,g2)
    c: Coincident(g2,g3)
    c: Coincident(g3,g0)
    c: Horizontal(g0)
    c: Vertical(g1)
    c: Vertical(g3)
    c: DistanceX(g0,g0) = 3
    c: DistanceY(g1,g1) = 5
    c: DistanceX(g2,g-1) = 55
    c: Horizontal(g2,g1)
    c: DistanceY(g-1,g0) = 20
FEATURE [PartDesign::Pad] Pad007
  BaseFeature = -> Pocket014
  Direction = (-1,0,0)
  Length = 110
  Length2 = 10
  Profile = -> Sketch019
  ReferenceAxis = -> Sketch019 [N_Axis]
  Type = 0
FEATURE [Sketcher::SketchObject] Sketch015
  FullyConstrained = true
  MapMode = 5
  Placement = pos=(0,59,0) rot=(0,0.707107,0.707107;3.14159rad)
  Support = -> [Pocket013]
FEATURE [PartDesign::Body] Body007  label="cono"
  Group = -> [Sketch037,Pad002,Sketch038,Pocket012,DatumPlane,Sketch008,Pocket001,Thickness001,Sketch014,Pocket013,Sketch015,Sketch016,Pad022,Sketch018,Pocket014,Sketch019,Pad007]
  Origin = -> Origin013
  Placement = pos=(243.9,-6e-14,96.9336) rot=(-0.621515,0.621515,0.476905;4.0316rad)
  Tip = -> Pad007
FEATURE [Sketcher::SketchObject] Sketch039
  FullyConstrained = false
  MapMode = 5
  Support = -> [XY_Plane014]
  sketch-geometry (20):
    g0: LineSegment StartX=54.5 StartY=57 StartZ=0 EndX=54.5 EndY=-57 EndZ=0
    g1: LineSegment StartX=54.5 StartY=-57 StartZ=0 EndX=-54.5 EndY=-57 EndZ=0
    g2: LineSegment StartX=-54.5 StartY=-57 StartZ=0 EndX=-54.5 EndY=57 EndZ=0
    g3: GeomPoint X=-30 Y=57 Z=0
    g4: GeomPoint X=30 Y=57 Z=0
    g5: ArcOfCircle CenterX=-30 CenterY=57 CenterZ=0 NormalX=0 NormalY=0 NormalZ=1 AngleXU=0 Radius=20 StartAngle=1.5708 EndAngle=3.14159
    g6: ArcOfCircle CenterX=30 CenterY=57 CenterZ=0 NormalX=0 NormalY=0 NormalZ=1 AngleXU=0 Radius=20 StartAngle=2.5e-15 EndAngle=1.5708
    g7: LineSegment StartX=30 StartY=77 StartZ=0 EndX=-30 EndY=77 EndZ=0
    g8: GeomPoint X=-50 Y=57 Z=0
    g9: GeomPoint X=50 Y=57 Z=0
    g10: LineSegment StartX=-54.5 StartY=57 StartZ=0 EndX=-50 EndY=57 EndZ=0
    g11: LineSegment StartX=54.5 StartY=57 StartZ=0 EndX=50 EndY=57 EndZ=0
    g12: ArcOfCircle CenterX=-30 CenterY=57 CenterZ=0 NormalX=0 NormalY=0 NormalZ=1 AngleXU=0 Radius=14.9762 StartAngle=1.56769 EndAngle=3.14159
    g13: ArcOfCircle CenterX=29.9509 CenterY=56.8139 CenterZ=0 NormalX=0 NormalY=0 NormalZ=1 AngleXU=0 Radius=14.9762 StartAngle=0.0124265 EndAngle=1.56769
    g14: LineSegment StartX=29.9974 StartY=71.79 StartZ=0 EndX=-29.9535 EndY=71.9761 EndZ=0
    g15: GeomPoint X=-44.9762 Y=57 Z=0
    g16: GeomPoint X=44.9259 Y=57 Z=0
    g17: LineSegment StartX=-44.9762 StartY=57 StartZ=0 EndX=-30 EndY=57 EndZ=0
    g18: LineSegment StartX=-30 StartY=57 StartZ=0 EndX=30 EndY=57 EndZ=0
    g19: LineSegment StartX=30 StartY=57 StartZ=0 EndX=44.9259 EndY=57 EndZ=0
  constraints (44):
    c: Coincident(g0,g1)
    c: Coincident(g1,g2)
    c: Horizontal(g1)
    c: Vertical(g0)
    c: DistanceX(g2,g0) = 109
    c: DistanceY(g0,g0) = 114
    c: Symmetric(g2,g0,g-2)
    c: Symmetric(g1,g2,g-1)
    c: Horizontal(g3,g2)
    c: DistanceX(g3,g4) = 60
    c: Symmetric(g3,g4,g-2)
    c: Tangent(g6,g7) = -1.5708
    c: Tangent(g7,g5) = -1.5708
    c: Equal(g5,g6)
    c: Coincident(g5,g3)
    c: Coincident(g6,g4)
    c: DistanceY(g6,g6) = 20
    c: PointOnObject(g8,g5)
    c: Horizontal(g8,g2)
    c: PointOnObject(g9,g6)
    c: Horizontal(g0,g9)
    c: Coincident(g10,g2)
    c: Coincident(g10,g8)
    c: Coincident(g11,g0)
    c: Coincident(g11,g9)
    c: PointOnObject(g5,g10)
    c: PointOnObject(g6,g11)
    c: Tangent(g13,g14) = -1.5708
    c: Tangent(g14,g12) = -1.5708
    c: Equal(g12,g13)
    c: Coincident(g12,g5)
    c: DistanceY(g6,g13) = 14.79
    c: PointOnObject(g15,g12)
    c: Horizontal(g5,g15)
    c: PointOnObject(g16,g13)
    c: Horizontal(g16,g6)
    c: Coincident(g17,g15)
    c: Coincident(g18,g17)
    c: Coincident(g18,g6)
    c: Horizontal(g18)
    c: Coincident(g19,g6)
    c: Coincident(g19,g16)
    c: PointOnObject(g12,g17)
    c: PointOnObject(g13,g19)
FEATURE [PartDesign::Pad] Pad006
  Direction = (0,0,1)
  Length = 3
  Length2 = 10
  Profile = -> Sketch039
  ReferenceAxis = -> Sketch039 [N_Axis]
  Type = 0
FEATURE [PartDesign::Plane] DatumPlane001
  Length = 133.171
  MapMode = 5
  Placement = pos=(0,0,3) rot=(0,0,1;0rad)
  ResizeMode = 0
  Support = -> [Pad006]
  Width = 158.171
FEATURE [Sketcher::SketchObject] Sketch020
  FullyConstrained = true
  MapMode = 5
  Placement = pos=(0,0,3) rot=(0,0,1;0rad)
  Support = -> [DatumPlane001]
  sketch-geometry (4):
    g0: LineSegment StartX=-54.5 StartY=57 StartZ=0 EndX=54.5 EndY=57 EndZ=0
    g1: LineSegment StartX=54.5 StartY=57 StartZ=0 EndX=54.5 EndY=53 EndZ=0
    g2: LineSegment StartX=54.5 StartY=53 StartZ=0 EndX=-54.5 EndY=53 EndZ=0
    g3: LineSegment StartX=-54.5 StartY=53 StartZ=0 EndX=-54.5 EndY=57 EndZ=0
  constraints (11):
    c: Coincident(g0,g1)
    c: Coincident(g1,g2)
    c: Coincident(g2,g3)
    c: Coincident(g3,g0)
    c: Horizontal(g0)
    c: Vertical(g1)
    c: Vertical(g3)
    c: DistanceY(g1,g1) = 4
    c: DistanceX(g0,g0) = 109
    c: Symmetric(g2,g1,g-2)
    c: DistanceY(g-1,g0) = 57
FEATURE [PartDesign::Pad] Pad008
  BaseFeature = -> Pad006
  Direction = (0,0,1)
  Length = 16
  Length2 = 10
  Profile = -> Sketch020
  ReferenceAxis = -> Sketch020 [N_Axis]
  Type = 0
FEATURE [PartDesign::Body] Body008
  Group = -> [Sketch039,Pad006,DatumPlane001,Sketch020,Pad008]
  Origin = -> Origin014
  Placement = pos=(243.316,-2.3e-14,99.8316) rot=(0.621515,-0.621515,-0.476905;2.25159rad)
  Tip = -> Pad008
FEATURE [Part::Compound] Compound001  label="soporte CAMARA"
  Links = -> [Part__Feature007,Part003,Part004,Body007,Body008]
  Placement = pos=(-122,69,53) rot=(-1,0,0;1.5708rad)
FEATURE [Sketcher::SketchObject] Sketch040
  ExternalGeometry = -> [Pocket011]
  FullyConstrained = true
  MapMode = 5
  Placement = pos=(-129,0,0) rot=(0.57735,-0.57735,-0.57735;2.0944rad)
  Support = -> [Pocket011]
  sketch-geometry (6):
    g0: LineSegment StartX=-60 StartY=67 StartZ=0 EndX=-57 EndY=67 EndZ=0
    g1: LineSegment StartX=-57 StartY=67 StartZ=0 EndX=-57 EndY=42 EndZ=0
    g2: LineSegment StartX=-57 StartY=42 StartZ=0 EndX=-60 EndY=42 EndZ=0
    g3: LineSegment StartX=-60 StartY=42 StartZ=0 EndX=-60 EndY=67 EndZ=0
    g4: LineSegment StartX=-60 StartY=42 StartZ=0 EndX=-65 EndY=42 EndZ=0
    g5: LineSegment StartX=-60 StartY=42 StartZ=0 EndX=-60 EndY=0 EndZ=0
  constraints (18):
    c: Coincident(g0,g1)
    c: Coincident(g1,g2)
    c: Coincident(g2,g3)
    c: Coincident(g3,g0)
    c: Horizontal(g0)
    c: Horizontal(g2)
    c: Vertical(g1)
    c: Vertical(g3)
    c: DistanceX(g0,g0) = 3
    c: DistanceY(g3,g3) = 25
    c: Coincident(g4,g2)
    c: PointOnObject(g4,g-3)
    c: Horizontal(g4)
    c: Coincident(g5,g2)
    c: PointOnObject(g5,g-1)
    c: Vertical(g5)
    c: DistanceX(g4,g4) = 5
    c: DistanceY(g5,g5) = 42
FEATURE [PartDesign::Pocket] Pocket015
  BaseFeature = -> Pocket011
  Direction = (1,0,0)
  Length = 5
  Length2 = 5
  Profile = -> Sketch040
  ReferenceAxis = -> Sketch040 [N_Axis]
  Type = 0
FEATURE [Sketcher::SketchObject] Sketch041
  ExternalGeometry = -> [Pocket015]
  FullyConstrained = false
  MapMode = 5
  Placement = pos=(129,0,0) rot=(0.57735,0.57735,0.57735;2.0944rad)
  Support = -> [Pocket015]
  sketch-geometry (2):
    g0: Circle CenterX=-58 CenterY=22.9132 CenterZ=0 NormalX=0 NormalY=0 NormalZ=1 AngleXU=0 Radius=5.5
    g1: LineSegment StartX=-58 StartY=22.9132 StartZ=0 EndX=-65 EndY=22.9132 EndZ=0
  constraints (5):
    c: Coincident(g1,g0)
    c: PointOnObject(g1,g-3)
    c: Horizontal(g1)
    c: Radius(g0) = 5.5
    c: Distance(g1) = 7
FEATURE [PartDesign::Pocket] Pocket016
  BaseFeature = -> Pocket015
  Direction = (-1,0,0)
  Length = 5
  Length2 = 5
  Profile = -> Sketch041
  ReferenceAxis = -> Sketch041 [N_Axis]
  Type = 0
FEATURE [Sketcher::SketchObject] Sketch042
  FullyConstrained = false
  MapMode = 5
  Placement = pos=(0,-69,0) rot=(1,0,0;1.5708rad)
  Support = -> [Pocket016]
  sketch-geometry (6):
    g0: LineSegment StartX=-124 StartY=40.0697 StartZ=0 EndX=-118 EndY=40.0697 EndZ=0
    g1: LineSegment StartX=-118 StartY=40.0697 StartZ=0 EndX=-118 EndY=24.0697 EndZ=0
    g2: LineSegment StartX=-118 StartY=24.0697 StartZ=0 EndX=-124 EndY=24.0697 EndZ=0
    g3: LineSegment StartX=-124 StartY=24.0697 StartZ=0 EndX=-124 EndY=40.0697 EndZ=0
    g4: LineSegment StartX=-124 StartY=40.0697 StartZ=0 EndX=-129 EndY=40.0697 EndZ=0
    g5: LineSegment StartX=-124 StartY=24.0697 StartZ=0 EndX=-124 EndY=0 EndZ=0
  constraints (16):
    c: Coincident(g0,g1)
    c: Coincident(g1,g2)
    c: Coincident(g2,g3)
    c: Coincident(g3,g0)
    c: Horizontal(g0)
    c: Horizontal(g2)
    c: Vertical(g1)
    c: Vertical(g3)
    c: Coincident(g4,g0)
    c: Horizontal(g4)
    c: Coincident(g5,g2)
    c: PointOnObject(g5,g-1)
    c: Vertical(g5)
    c: DistanceX(g4,g4) = 5
    c: DistanceX(g0,g0) = 6
    c: DistanceY(g1,g1) = 16
FEATURE [PartDesign::Pocket] Pocket017
  BaseFeature = -> Pocket016
  Direction = (0,1,-2e-16)
  Length = 4
  Length2 = 5
  Profile = -> Sketch042
  ReferenceAxis = -> Sketch042 [N_Axis]
  Type = 0
FEATURE [PartDesign::Body] Body  label="CAJA"
  Group = -> [Sketch,Pad,Thickness,Sketch021,Pad017,Sketch022,Pocket,Sketch023,Pad018,Sketch024,Pocket004,Sketch029,Pocket006,Sketch031,Pocket008,Sketch032,Pocket009,Sketch033,Pocket010,Sketch034,Pocket011,Sketch040,Pocket015,Sketch041,Pocket016,Sketch042,Pocket017]
  Origin = -> Origin001
  Tip = -> Pocket017
FEATURE [App::Part] Part
  Group = -> [Body,Body003,Body004]
  Origin = -> Origin
